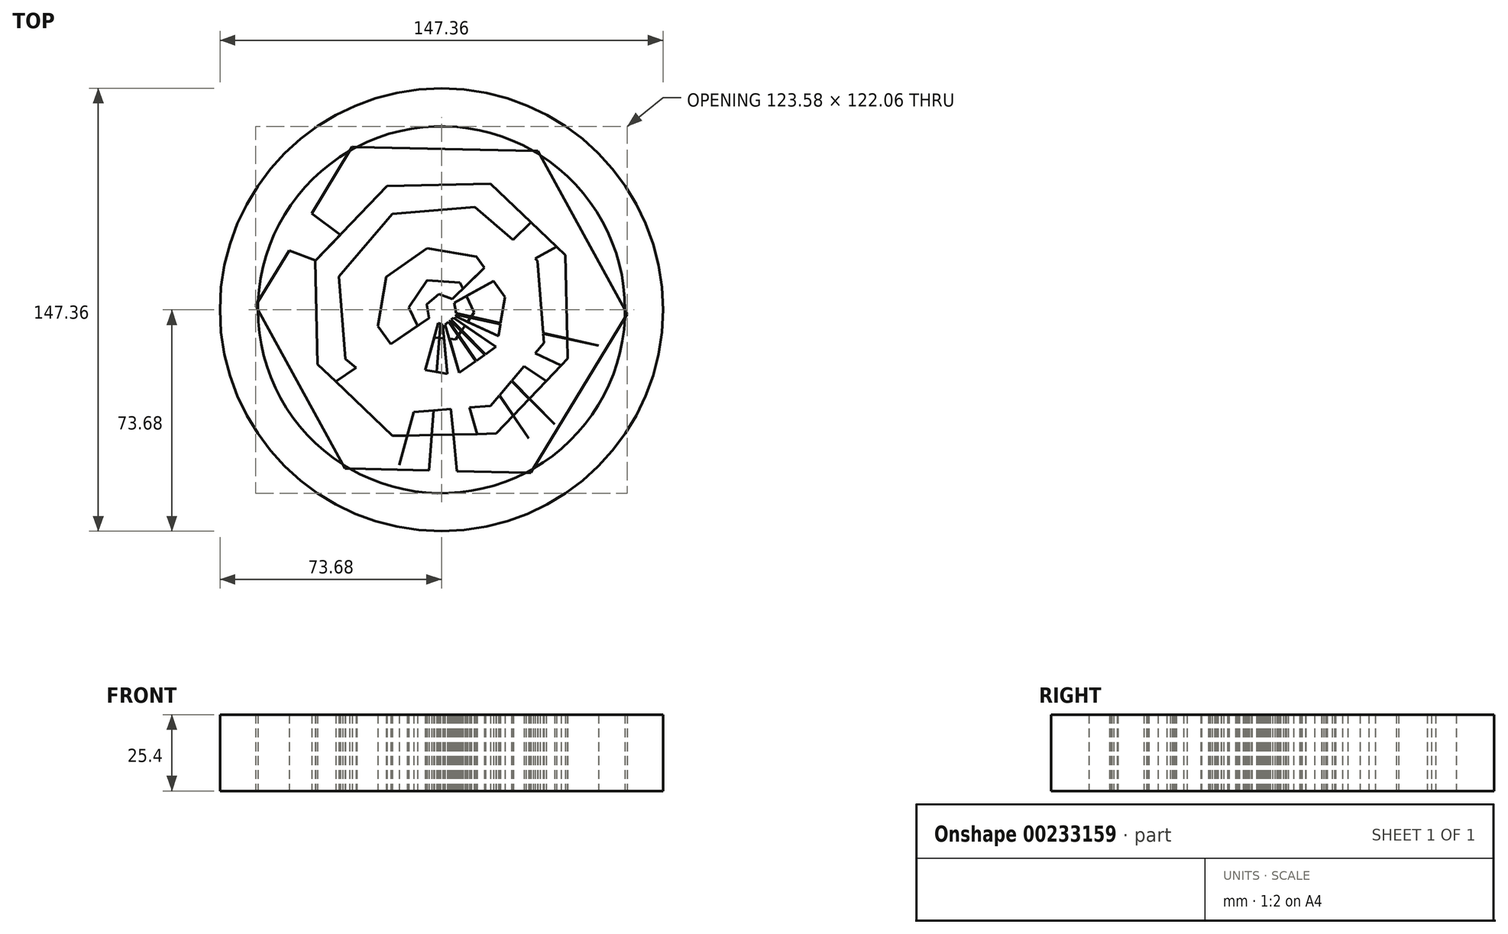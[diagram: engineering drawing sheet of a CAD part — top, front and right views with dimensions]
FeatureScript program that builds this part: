
annotation { "Feature Type Name" : "Feature", "Feature Type Description" : "" }
export const myFeature = defineFeature(function(context is Context, id is Id, definition is map)
    precondition{}
    {
        {
            var Q0;
            Q0=qCreatedBy(makeId("Top.planeOp"),FACE);
            var sketch = newSketch(context, id + "F0", { "sketchPlane" : qUnion([Q0])});
            skCircle(sketch, "E0", {"center": v(0, 0) * mm, "radius": 73.68 * mm});
            skCircle(sketch, "E1", {"center": v(0, 0) * mm, "radius": 61.04 * mm});
            skCircle(sketch, "E2.cCircle", {"center": v(0, 0) * mm, "radius": 53.52 * mm, "construction": true});
            skLineSegment(sketch, "E2.0", {"start": v(61.79, -1.37) * mm, "end": v(29.7, -54.2) * mm});
            skLineSegment(sketch, "E2.1", {"start": v(29.7, -54.2) * mm, "end": v(-32.08, -52.83) * mm});
            skLineSegment(sketch, "E2.2", {"start": v(-32.08, -52.83) * mm, "end": v(-61.79, 1.37) * mm});
            skLineSegment(sketch, "E2.3", {"start": v(-61.79, 1.37) * mm, "end": v(-29.7, 54.2) * mm});
            skLineSegment(sketch, "E2.4", {"start": v(-29.7, 54.2) * mm, "end": v(32.08, 52.83) * mm});
            skLineSegment(sketch, "E2.5", {"start": v(32.08, 52.83) * mm, "end": v(61.79, -1.37) * mm});
            skPoint(sketch, "E2.0.midPoint", {"position": v(45.75, -27.78) * mm});
            skLineSegment(sketch, "E3", {"start": v(0, 0) * mm, "end": v(-34.13, 41.23) * mm});
            skLineSegment(sketch, "E4", {"start": v(-34.13, 41.23) * mm, "end": v(-23.24, 48.21) * mm});
            skLineSegment(sketch, "E5", {"start": v(-23.24, 48.21) * mm, "end": v(0, 0) * mm});
            skLineSegment(sketch, "E6", {"start": v(-10.55, 52.47) * mm, "end": v(0, 0) * mm});
            skLineSegment(sketch, "E7", {"start": v(0, 0) * mm, "end": v(15.37, 51.27) * mm});
            skLineSegment(sketch, "E8", {"start": v(15.37, 51.27) * mm, "end": v(28.63, 45.22) * mm});
            skLineSegment(sketch, "E9", {"start": v(28.63, 45.22) * mm, "end": v(0, 0) * mm});
            skLineSegment(sketch, "E10", {"start": v(0, 0) * mm, "end": v(38.25, 37.44) * mm});
            skLineSegment(sketch, "E11", {"start": v(38.25, 37.44) * mm, "end": v(0, 0) * mm});
            skLineSegment(sketch, "E12", {"start": v(0, 0) * mm, "end": v(46.93, 25.73) * mm});
            skLineSegment(sketch, "E13", {"start": v(46.93, 25.73) * mm, "end": v(51.95, 12.87) * mm});
            skLineSegment(sketch, "E14", {"start": v(51.95, 12.87) * mm, "end": v(0, 0) * mm});
            skLineSegment(sketch, "E15", {"start": v(0, 0) * mm, "end": v(-43.18, 32) * mm});
            skLineSegment(sketch, "E16", {"start": v(-43.18, 32) * mm, "end": v(-50.62, 19.76) * mm});
            skLineSegment(sketch, "E17", {"start": v(-50.62, 19.76) * mm, "end": v(0, 0) * mm});
            skLineSegment(sketch, "E18", {"start": v(-53.16, 6.18) * mm, "end": v(0, 0) * mm});
            skLineSegment(sketch, "E19", {"start": v(-53.02, -7.3) * mm, "end": v(0, 0) * mm});
            skLineSegment(sketch, "E20", {"start": v(8.49, 53.35) * mm, "end": v(0, 0) * mm});
            skLineSegment(sketch, "E21", {"start": v(-1.18, 53.51) * mm, "end": v(0, 0) * mm});
            skPoint(sketch, "E21.startSnap0", {"position": v(1.18, 53.51) * mm});
            skLineSegment(sketch, "E22", {"start": v(-49.6, -20.1) * mm, "end": v(0, 0) * mm});
            skLineSegment(sketch, "E23", {"start": v(0, 0) * mm, "end": v(-44.46, -30.23) * mm});
            skLineSegment(sketch, "E24", {"start": v(-44.46, -30.23) * mm, "end": v(0, 0) * mm});
            skLineSegment(sketch, "E25", {"start": v(0, 0) * mm, "end": v(-38.05, -37.64) * mm});
            skLineSegment(sketch, "E26", {"start": v(-38.05, -37.64) * mm, "end": v(0, 0) * mm});
            skLineSegment(sketch, "E27", {"start": v(0, 0) * mm, "end": v(-30.17, -44.21) * mm});
            skLineSegment(sketch, "E28", {"start": v(-30.17, -44.21) * mm, "end": v(0, 0) * mm});
            skLineSegment(sketch, "E29", {"start": v(0, 0) * mm, "end": v(-22.6, -48.52) * mm});
            skLineSegment(sketch, "E30", {"start": v(-22.6, -48.52) * mm, "end": v(0, 0) * mm});
            skLineSegment(sketch, "E31", {"start": v(0, -0.62) * mm, "end": v(-14.1, -51.63) * mm});
            skLineSegment(sketch, "E32", {"start": v(-14.1, -51.63) * mm, "end": v(0, 0) * mm});
            skLineSegment(sketch, "E33", {"start": v(0, 0) * mm, "end": v(-4.14, -53.44) * mm});
            skLineSegment(sketch, "E34", {"start": v(-4.14, -53.44) * mm, "end": v(0, -0.62) * mm});
            skLineSegment(sketch, "E35", {"start": v(0, 0) * mm, "end": v(52.18, -11.9) * mm});
            skLineSegment(sketch, "E36", {"start": v(52.18, -11.9) * mm, "end": v(0, -0.62) * mm});
            skLineSegment(sketch, "E37", {"start": v(0, 0) * mm, "end": v(48.52, -22.6) * mm});
            skLineSegment(sketch, "E38", {"start": v(48.52, -22.6) * mm, "end": v(0, 0) * mm});
            skLineSegment(sketch, "E39", {"start": v(0, 0) * mm, "end": v(37.64, -38.05) * mm});
            skLineSegment(sketch, "E40", {"start": v(37.64, -38.05) * mm, "end": v(0, -0.62) * mm});
            skLineSegment(sketch, "E41", {"start": v(0, 0) * mm, "end": v(29.06, -42.74) * mm});
            skLineSegment(sketch, "E42", {"start": v(29.06, -42.74) * mm, "end": v(0, -0.62) * mm});
            skLineSegment(sketch, "E43", {"start": v(0, -0.62) * mm, "end": v(14.85, -51.42) * mm});
            skLineSegment(sketch, "E44", {"start": v(14.85, -51.42) * mm, "end": v(0, -0.62) * mm});
            skLineSegment(sketch, "E45", {"start": v(0, -0.62) * mm, "end": v(5.17, -53.65) * mm});
            skLineSegment(sketch, "E46", {"start": v(5.17, -53.65) * mm, "end": v(0, -0.62) * mm});
            skLineSegment(sketch, "E47", {"start": v(53.52, -0.62) * mm, "end": v(0, 0) * mm});
            skLineSegment(sketch, "E48", {"start": v(0, 0) * mm, "end": v(44.21, -30.17) * mm});
            skLineSegment(sketch, "E49", {"start": v(44.21, -30.17) * mm, "end": v(0, 0) * mm});
            skLineSegment(sketch, "E50", {"start": v(-53.52, -0.62) * mm, "end": v(0, 0) * mm});
            skCircle(sketch, "E51.cCircle", {"center": v(0, 0) * mm, "radius": 41.58 * mm, "construction": true});
            skLineSegment(sketch, "E51.0", {"start": v(18.14, -41.2) * mm, "end": v(-16.3, -41.95) * mm});
            skLineSegment(sketch, "E51.1", {"start": v(-16.3, -41.95) * mm, "end": v(-41.2, -18.14) * mm});
            skLineSegment(sketch, "E51.2", {"start": v(-41.2, -18.14) * mm, "end": v(-41.95, 16.3) * mm});
            skLineSegment(sketch, "E51.3", {"start": v(-41.95, 16.3) * mm, "end": v(-18.14, 41.2) * mm});
            skLineSegment(sketch, "E51.4", {"start": v(-18.14, 41.2) * mm, "end": v(16.3, 41.95) * mm});
            skLineSegment(sketch, "E51.5", {"start": v(16.3, 41.95) * mm, "end": v(41.2, 18.14) * mm});
            skLineSegment(sketch, "E51.6", {"start": v(41.2, 18.14) * mm, "end": v(41.95, -16.3) * mm});
            skLineSegment(sketch, "E51.7", {"start": v(41.95, -16.3) * mm, "end": v(18.14, -41.2) * mm});
            skPoint(sketch, "E51.0.midPoint", {"position": v(0.92, -41.57) * mm});
            skCircle(sketch, "E52.cCircle", {"center": v(0, 0) * mm, "radius": 33.14 * mm, "construction": true});
            skLineSegment(sketch, "E52.0", {"start": v(34.13, -11.05) * mm, "end": v(16.32, -31.95) * mm});
            skLineSegment(sketch, "E52.1", {"start": v(16.32, -31.95) * mm, "end": v(-11.05, -34.13) * mm});
            skLineSegment(sketch, "E52.2", {"start": v(-11.05, -34.13) * mm, "end": v(-31.95, -16.32) * mm});
            skLineSegment(sketch, "E52.3", {"start": v(-31.95, -16.32) * mm, "end": v(-34.13, 11.05) * mm});
            skLineSegment(sketch, "E52.4", {"start": v(-34.13, 11.05) * mm, "end": v(-16.32, 31.95) * mm});
            skLineSegment(sketch, "E52.5", {"start": v(-16.32, 31.95) * mm, "end": v(11.05, 34.13) * mm});
            skLineSegment(sketch, "E52.6", {"start": v(11.05, 34.13) * mm, "end": v(31.95, 16.32) * mm});
            skLineSegment(sketch, "E52.7", {"start": v(31.95, 16.32) * mm, "end": v(34.13, -11.05) * mm});
            skPoint(sketch, "E52.0.midPoint", {"position": v(25.22, -21.5) * mm});
            skCircle(sketch, "E53.cCircle", {"center": v(0, -0.62) * mm, "radius": 20.03 * mm, "construction": true});
            skLineSegment(sketch, "E53.0", {"start": v(18.32, -12.2) * mm, "end": v(4.77, -21.77) * mm});
            skLineSegment(sketch, "E53.1", {"start": v(4.77, -21.77) * mm, "end": v(-11.58, -18.94) * mm});
            skLineSegment(sketch, "E53.2", {"start": v(-11.58, -18.94) * mm, "end": v(-21.14, -5.39) * mm});
            skLineSegment(sketch, "E53.3", {"start": v(-21.14, -5.39) * mm, "end": v(-18.32, 10.96) * mm});
            skLineSegment(sketch, "E53.4", {"start": v(-18.32, 10.96) * mm, "end": v(-4.77, 20.52) * mm});
            skLineSegment(sketch, "E53.5", {"start": v(-4.77, 20.52) * mm, "end": v(11.58, 17.7) * mm});
            skLineSegment(sketch, "E53.6", {"start": v(11.58, 17.7) * mm, "end": v(21.14, 4.15) * mm});
            skLineSegment(sketch, "E53.7", {"start": v(21.14, 4.15) * mm, "end": v(18.32, -12.2) * mm});
            skPoint(sketch, "E53.0.midPoint", {"position": v(11.55, -16.98) * mm});
            skCircle(sketch, "E54.cCircle", {"center": v(0, 0) * mm, "radius": 9.46 * mm, "construction": true});
            skLineSegment(sketch, "E54.0", {"start": v(10.89, -0.82) * mm, "end": v(4.73, -9.84) * mm});
            skLineSegment(sketch, "E54.1", {"start": v(4.73, -9.84) * mm, "end": v(-6.15, -9.02) * mm});
            skLineSegment(sketch, "E54.2", {"start": v(-6.15, -9.02) * mm, "end": v(-10.89, 0.82) * mm});
            skLineSegment(sketch, "E54.3", {"start": v(-10.89, 0.82) * mm, "end": v(-4.73, 9.84) * mm});
            skLineSegment(sketch, "E54.4", {"start": v(-4.73, 9.84) * mm, "end": v(6.15, 9.02) * mm});
            skLineSegment(sketch, "E54.5", {"start": v(6.15, 9.02) * mm, "end": v(10.89, -0.82) * mm});
            skPoint(sketch, "E54.0.midPoint", {"position": v(7.81, -5.33) * mm});
            skCircle(sketch, "E55.cCircle", {"center": v(0, 0) * mm, "radius": 4.56 * mm, "construction": true});
            skLineSegment(sketch, "E55.0", {"start": v(4.93, -1.83) * mm, "end": v(0.88, -5.19) * mm});
            skLineSegment(sketch, "E55.1", {"start": v(0.88, -5.19) * mm, "end": v(-4.05, -3.35) * mm});
            skLineSegment(sketch, "E55.2", {"start": v(-4.05, -3.35) * mm, "end": v(-4.93, 1.83) * mm});
            skLineSegment(sketch, "E55.3", {"start": v(-4.93, 1.83) * mm, "end": v(-0.88, 5.19) * mm});
            skLineSegment(sketch, "E55.4", {"start": v(-0.88, 5.19) * mm, "end": v(4.05, 3.35) * mm});
            skLineSegment(sketch, "E55.5", {"start": v(4.05, 3.35) * mm, "end": v(4.93, -1.83) * mm});
            skPoint(sketch, "E55.0.midPoint", {"position": v(2.9, -3.5) * mm});
            skSolve(sketch);
        }
        {
            var Q0;
            {var subQ0=sQuery(id+"F0.wireOp",EDGE,"E53.3");var subQ3=sQuery(id+"F0.wireOp",EDGE,"E19");var subQ4=makeQuery(id+"F0.imprint","INTERSECT",VERTEX,{"derivedFrom":[subQ3,subQ0]});Q0=makeQuery(id+"F0.imprint","IMPRINT",FACE,{"disambiguationData":[TD([[makeQuery(id+"F0.imprint","IMPRINT",EDGE,{"disambiguationData":[TD([[subQ4,-1.0]])],"derivedFrom":subQ3}),-1.0]])]});}
            var Q1;
            {var subQ0=sQuery(id+"F0.wireOp",EDGE,"E53.3");var subQ1=sQuery(id+"F0.wireOp",EDGE,"E19");var subQ2=makeQuery(id+"F0.imprint","INTERSECT",VERTEX,{"derivedFrom":[subQ1,subQ0]});Q1=makeQuery(id+"F0.imprint","IMPRINT",FACE,{"disambiguationData":[TD([[makeQuery(id+"F0.imprint","IMPRINT",EDGE,{"disambiguationData":[TD([[subQ2,-1.0]])],"derivedFrom":subQ1}),1.0]])]});}
            var Q2;
            {var subQ5=sQuery(id+"F0.wireOp",EDGE,"E53.3");var subQ6=sQuery(id+"F0.wireOp",EDGE,"E18");var subQ7=makeQuery(id+"F0.imprint","INTERSECT",VERTEX,{"derivedFrom":[subQ6,subQ5]});Q2=makeQuery(id+"F0.imprint","IMPRINT",FACE,{"disambiguationData":[TD([[makeQuery(id+"F0.imprint","IMPRINT",EDGE,{"disambiguationData":[TD([[subQ7,-1.0]])],"derivedFrom":subQ6}),-1.0]])]});}
            var Q3;
            {var subQ0=sQuery(id+"F0.wireOp",EDGE,"E53.3");var subQ1=sQuery(id+"F0.wireOp",EDGE,"E17");var subQ2=makeQuery(id+"F0.imprint","INTERSECT",VERTEX,{"derivedFrom":[subQ1,subQ0]});Q3=makeQuery(id+"F0.imprint","IMPRINT",FACE,{"disambiguationData":[TD([[makeQuery(id+"F0.imprint","IMPRINT",EDGE,{"disambiguationData":[TD([[subQ2,-1.0]])],"derivedFrom":subQ1}),-1.0]])]});}
            var Q4;
            {var subQ3=sQuery(id+"F0.wireOp",EDGE,"E15");var subQ7=sQuery(id+"F0.wireOp",EDGE,"E54.3");var subQ9=makeQuery(id+"F0.imprint","INTERSECT",VERTEX,{"derivedFrom":[subQ3,subQ7]});Q4=makeQuery(id+"F0.imprint","IMPRINT",FACE,{"disambiguationData":[TD([[makeQuery(id+"F0.imprint","IMPRINT",EDGE,{"disambiguationData":[TD([[subQ9,-1.0]])],"derivedFrom":subQ3}),1.0]])]});}
            var Q5;
            {var subQ0=sQuery(id+"F0.wireOp",EDGE,"E54.3");var subQ1=sQuery(id+"F0.wireOp",EDGE,"E3");var subQ2=makeQuery(id+"F0.imprint","INTERSECT",VERTEX,{"derivedFrom":[subQ1,subQ0]});Q5=makeQuery(id+"F0.imprint","IMPRINT",FACE,{"disambiguationData":[TD([[makeQuery(id+"F0.imprint","IMPRINT",EDGE,{"disambiguationData":[TD([[subQ2,-1.0]])],"derivedFrom":subQ1}),1.0]])]});}
            var Q6;
            {var subQ0=sQuery(id+"F0.wireOp",EDGE,"E54.3");var subQ1=sQuery(id+"F0.wireOp",EDGE,"E3");var subQ2=makeQuery(id+"F0.imprint","INTERSECT",VERTEX,{"derivedFrom":[subQ1,subQ0]});Q6=makeQuery(id+"F0.imprint","IMPRINT",FACE,{"disambiguationData":[TD([[makeQuery(id+"F0.imprint","IMPRINT",EDGE,{"disambiguationData":[TD([[subQ2,-1.0]])],"derivedFrom":subQ1}),-1.0]])]});}
            var Q7;
            {var subQ1=sQuery(id+"F0.wireOp",EDGE,"E53.4");var subQ7=sQuery(id+"F0.wireOp",EDGE,"E5");var subQ8=makeQuery(id+"F0.imprint","INTERSECT",VERTEX,{"derivedFrom":[subQ7,subQ1]});Q7=makeQuery(id+"F0.imprint","IMPRINT",FACE,{"disambiguationData":[TD([[makeQuery(id+"F0.imprint","IMPRINT",EDGE,{"disambiguationData":[TD([[subQ8,-1.0]])],"derivedFrom":subQ7}),1.0]])]});}
            var Q8;
            {var subQ0=sQuery(id+"F0.wireOp",EDGE,"E53.5");var subQ1=sQuery(id+"F0.wireOp",EDGE,"E6");var subQ2=makeQuery(id+"F0.imprint","INTERSECT",VERTEX,{"derivedFrom":[subQ1,subQ0]});Q8=makeQuery(id+"F0.imprint","IMPRINT",FACE,{"disambiguationData":[TD([[makeQuery(id+"F0.imprint","IMPRINT",EDGE,{"disambiguationData":[TD([[subQ2,-1.0]])],"derivedFrom":subQ1}),1.0]])]});}
            var Q9;
            {var subQ0=sQuery(id+"F0.wireOp",EDGE,"E53.5");var subQ1=sQuery(id+"F0.wireOp",EDGE,"E20");var subQ2=makeQuery(id+"F0.imprint","INTERSECT",VERTEX,{"derivedFrom":[subQ1,subQ0]});Q9=makeQuery(id+"F0.imprint","IMPRINT",FACE,{"disambiguationData":[TD([[makeQuery(id+"F0.imprint","IMPRINT",EDGE,{"disambiguationData":[TD([[subQ2,-1.0]])],"derivedFrom":subQ1}),-1.0]])]});}
            var Q10;
            {var subQ0=sQuery(id+"F0.wireOp",EDGE,"E54.4");var subQ1=sQuery(id+"F0.wireOp",EDGE,"E7");var subQ2=makeQuery(id+"F0.imprint","INTERSECT",VERTEX,{"derivedFrom":[subQ1,subQ0]});Q10=makeQuery(id+"F0.imprint","IMPRINT",FACE,{"disambiguationData":[TD([[makeQuery(id+"F0.imprint","IMPRINT",EDGE,{"disambiguationData":[TD([[subQ2,-1.0]])],"derivedFrom":subQ1}),1.0]])]});}
            var Q11;
            {var subQ0=sQuery(id+"F0.wireOp",EDGE,"E54.4");var subQ1=sQuery(id+"F0.wireOp",EDGE,"E7");var subQ2=makeQuery(id+"F0.imprint","INTERSECT",VERTEX,{"derivedFrom":[subQ1,subQ0]});Q11=makeQuery(id+"F0.imprint","IMPRINT",FACE,{"disambiguationData":[TD([[makeQuery(id+"F0.imprint","IMPRINT",EDGE,{"disambiguationData":[TD([[subQ2,-1.0]])],"derivedFrom":subQ1}),-1.0]])]});}
            var Q12;
            {var subQ1=sQuery(id+"F0.wireOp",EDGE,"E53.5");var subQ5=sQuery(id+"F0.wireOp",EDGE,"E9");var subQ6=makeQuery(id+"F0.imprint","INTERSECT",VERTEX,{"derivedFrom":[subQ5,subQ1]});Q12=makeQuery(id+"F0.imprint","IMPRINT",FACE,{"disambiguationData":[TD([[makeQuery(id+"F0.imprint","IMPRINT",EDGE,{"disambiguationData":[TD([[subQ6,-1.0]])],"derivedFrom":subQ5}),1.0]])]});}
            var Q13;
            {var subQ0=sQuery(id+"F0.wireOp",EDGE,"E53.6");var subQ1=sQuery(id+"F0.wireOp",EDGE,"E11");var subQ2=makeQuery(id+"F0.imprint","INTERSECT",VERTEX,{"derivedFrom":[subQ1,subQ0]});Q13=makeQuery(id+"F0.imprint","IMPRINT",FACE,{"disambiguationData":[TD([[makeQuery(id+"F0.imprint","IMPRINT",EDGE,{"disambiguationData":[TD([[subQ2,-1.0]])],"derivedFrom":subQ1}),1.0]])]});}
            var Q14;
            {var subQ1=sQuery(id+"F0.wireOp",EDGE,"E54.0");var subQ3=sQuery(id+"F0.wireOp",EDGE,"E35");var subQ4=makeQuery(id+"F0.imprint","INTERSECT",VERTEX,{"derivedFrom":[subQ3,subQ1]});Q14=makeQuery(id+"F0.imprint","IMPRINT",FACE,{"disambiguationData":[TD([[makeQuery(id+"F0.imprint","IMPRINT",EDGE,{"disambiguationData":[TD([[subQ4,-1.0]])],"derivedFrom":subQ3}),1.0]])]});}
            var Q15;
            {var subQ0=sQuery(id+"F0.wireOp",EDGE,"E54.5");var subQ1=sQuery(id+"F0.wireOp",EDGE,"E12");var subQ2=makeQuery(id+"F0.imprint","INTERSECT",VERTEX,{"derivedFrom":[subQ1,subQ0]});Q15=makeQuery(id+"F0.imprint","IMPRINT",FACE,{"disambiguationData":[TD([[makeQuery(id+"F0.imprint","IMPRINT",EDGE,{"disambiguationData":[TD([[subQ2,-1.0]])],"derivedFrom":subQ1}),-1.0]])]});}
            var Q16;
            {var subQ1=sQuery(id+"F0.wireOp",EDGE,"E53.6");var subQ3=sQuery(id+"F0.wireOp",EDGE,"E14");var subQ4=makeQuery(id+"F0.imprint","INTERSECT",VERTEX,{"derivedFrom":[subQ3,subQ1]});Q16=makeQuery(id+"F0.imprint","IMPRINT",FACE,{"disambiguationData":[TD([[makeQuery(id+"F0.imprint","IMPRINT",EDGE,{"disambiguationData":[TD([[subQ4,-1.0]])],"derivedFrom":subQ3}),1.0]])]});}
            var Q17;
            {var subQ5=sQuery(id+"F0.wireOp",EDGE,"E35");var subQ7=sQuery(id+"F0.wireOp",EDGE,"E55.5");var subQ9=makeQuery(id+"F0.imprint","INTERSECT",VERTEX,{"derivedFrom":[subQ5,subQ7]});Q17=makeQuery(id+"F0.imprint","IMPRINT",FACE,{"disambiguationData":[TD([[makeQuery(id+"F0.imprint","IMPRINT",EDGE,{"disambiguationData":[TD([[subQ9,-1.0]])],"derivedFrom":subQ5}),1.0]])]});}
            var Q18;
            {var subQ0=sQuery(id+"F0.wireOp",EDGE,"E54.5");var subQ1=sQuery(id+"F0.wireOp",EDGE,"E14");var subQ2=makeQuery(id+"F0.imprint","INTERSECT",VERTEX,{"derivedFrom":[subQ1,subQ0]});Q18=makeQuery(id+"F0.imprint","IMPRINT",FACE,{"disambiguationData":[TD([[makeQuery(id+"F0.imprint","IMPRINT",EDGE,{"disambiguationData":[TD([[subQ2,-1.0]])],"derivedFrom":subQ1}),1.0]])]});}
            var Q19;
            {var subQ0=sQuery(id+"F0.wireOp",EDGE,"E55.5");var subQ1=sQuery(id+"F0.wireOp",EDGE,"E12");var subQ2=makeQuery(id+"F0.imprint","INTERSECT",VERTEX,{"derivedFrom":[subQ1,subQ0]});Q19=makeQuery(id+"F0.imprint","IMPRINT",FACE,{"disambiguationData":[TD([[makeQuery(id+"F0.imprint","IMPRINT",EDGE,{"disambiguationData":[TD([[subQ2,-1.0]])],"derivedFrom":subQ1}),-1.0]])]});}
            var Q20;
            {var subQ3=sQuery(id+"F0.wireOp",EDGE,"E11");var subQ5=sQuery(id+"F0.wireOp",EDGE,"E54.5");var subQ6=makeQuery(id+"F0.imprint","INTERSECT",VERTEX,{"derivedFrom":[subQ3,subQ5]});Q20=makeQuery(id+"F0.imprint","IMPRINT",FACE,{"disambiguationData":[TD([[makeQuery(id+"F0.imprint","IMPRINT",EDGE,{"disambiguationData":[TD([[subQ6,-1.0]])],"derivedFrom":subQ3}),1.0]])]});}
            var Q21;
            {var subQ1=sQuery(id+"F0.wireOp",EDGE,"E54.4");var subQ6=sQuery(id+"F0.wireOp",EDGE,"E9");var subQ9=makeQuery(id+"F0.imprint","INTERSECT",VERTEX,{"derivedFrom":[subQ6,subQ1]});Q21=makeQuery(id+"F0.imprint","IMPRINT",FACE,{"disambiguationData":[TD([[makeQuery(id+"F0.imprint","IMPRINT",EDGE,{"disambiguationData":[TD([[subQ9,-1.0]])],"derivedFrom":subQ6}),1.0]])]});}
            var Q22;
            {var subQ0=sQuery(id+"F0.wireOp",EDGE,"E55.4");var subQ1=sQuery(id+"F0.wireOp",EDGE,"E7");var subQ2=makeQuery(id+"F0.imprint","INTERSECT",VERTEX,{"derivedFrom":[subQ1,subQ0]});Q22=makeQuery(id+"F0.imprint","IMPRINT",FACE,{"disambiguationData":[TD([[makeQuery(id+"F0.imprint","IMPRINT",EDGE,{"disambiguationData":[TD([[subQ2,-1.0]])],"derivedFrom":subQ1}),-1.0]])]});}
            var Q23;
            {var subQ0=sQuery(id+"F0.wireOp",EDGE,"E55.4");var subQ1=sQuery(id+"F0.wireOp",EDGE,"E7");var subQ2=makeQuery(id+"F0.imprint","INTERSECT",VERTEX,{"derivedFrom":[subQ1,subQ0]});Q23=makeQuery(id+"F0.imprint","IMPRINT",FACE,{"disambiguationData":[TD([[makeQuery(id+"F0.imprint","IMPRINT",EDGE,{"disambiguationData":[TD([[subQ2,-1.0]])],"derivedFrom":subQ1}),1.0]])]});}
            var Q24;
            {var subQ0=sQuery(id+"F0.wireOp",EDGE,"E54.4");var subQ1=sQuery(id+"F0.wireOp",EDGE,"E20");var subQ2=makeQuery(id+"F0.imprint","INTERSECT",VERTEX,{"derivedFrom":[subQ1,subQ0]});Q24=makeQuery(id+"F0.imprint","IMPRINT",FACE,{"disambiguationData":[TD([[makeQuery(id+"F0.imprint","IMPRINT",EDGE,{"disambiguationData":[TD([[subQ2,-1.0]])],"derivedFrom":subQ1}),-1.0]])]});}
            var Q25;
            {var subQ3=sQuery(id+"F0.wireOp",EDGE,"E6");var subQ5=sQuery(id+"F0.wireOp",EDGE,"E54.4");var subQ6=makeQuery(id+"F0.imprint","INTERSECT",VERTEX,{"derivedFrom":[subQ3,subQ5]});Q25=makeQuery(id+"F0.imprint","IMPRINT",FACE,{"disambiguationData":[TD([[makeQuery(id+"F0.imprint","IMPRINT",EDGE,{"disambiguationData":[TD([[subQ6,-1.0]])],"derivedFrom":subQ3}),1.0]])]});}
            var Q26;
            {var subQ1=sQuery(id+"F0.wireOp",EDGE,"E54.3");var subQ6=sQuery(id+"F0.wireOp",EDGE,"E5");var subQ9=makeQuery(id+"F0.imprint","INTERSECT",VERTEX,{"derivedFrom":[subQ6,subQ1]});Q26=makeQuery(id+"F0.imprint","IMPRINT",FACE,{"disambiguationData":[TD([[makeQuery(id+"F0.imprint","IMPRINT",EDGE,{"disambiguationData":[TD([[subQ9,-1.0]])],"derivedFrom":subQ6}),1.0]])]});}
            var Q27;
            {var subQ0=sQuery(id+"F0.wireOp",EDGE,"E55.3");var subQ1=sQuery(id+"F0.wireOp",EDGE,"E3");var subQ2=makeQuery(id+"F0.imprint","INTERSECT",VERTEX,{"derivedFrom":[subQ1,subQ0]});Q27=makeQuery(id+"F0.imprint","IMPRINT",FACE,{"disambiguationData":[TD([[makeQuery(id+"F0.imprint","IMPRINT",EDGE,{"disambiguationData":[TD([[subQ2,-1.0]])],"derivedFrom":subQ1}),-1.0]])]});}
            var Q28;
            {var subQ0=sQuery(id+"F0.wireOp",EDGE,"E55.3");var subQ1=sQuery(id+"F0.wireOp",EDGE,"E3");var subQ2=makeQuery(id+"F0.imprint","INTERSECT",VERTEX,{"derivedFrom":[subQ1,subQ0]});Q28=makeQuery(id+"F0.imprint","IMPRINT",FACE,{"disambiguationData":[TD([[makeQuery(id+"F0.imprint","IMPRINT",EDGE,{"disambiguationData":[TD([[subQ2,-1.0]])],"derivedFrom":subQ1}),1.0]])]});}
            var Q29;
            {var subQ0=sQuery(id+"F0.wireOp",EDGE,"E55.3");var subQ1=sQuery(id+"F0.wireOp",EDGE,"E15");var subQ2=makeQuery(id+"F0.imprint","INTERSECT",VERTEX,{"derivedFrom":[subQ1,subQ0]});Q29=makeQuery(id+"F0.imprint","IMPRINT",FACE,{"disambiguationData":[TD([[makeQuery(id+"F0.imprint","IMPRINT",EDGE,{"disambiguationData":[TD([[subQ2,-1.0]])],"derivedFrom":subQ1}),1.0]])]});}
            var Q30;
            {var subQ0=sQuery(id+"F0.wireOp",EDGE,"E54.3");var subQ1=sQuery(id+"F0.wireOp",EDGE,"E17");var subQ2=makeQuery(id+"F0.imprint","INTERSECT",VERTEX,{"derivedFrom":[subQ1,subQ0]});Q30=makeQuery(id+"F0.imprint","IMPRINT",FACE,{"disambiguationData":[TD([[makeQuery(id+"F0.imprint","IMPRINT",EDGE,{"disambiguationData":[TD([[subQ2,-1.0]])],"derivedFrom":subQ1}),-1.0]])]});}
            var Q31;
            {var subQ0=sQuery(id+"F0.wireOp",EDGE,"E54.2");var subQ1=sQuery(id+"F0.wireOp",EDGE,"E19");var subQ2=makeQuery(id+"F0.imprint","INTERSECT",VERTEX,{"derivedFrom":[subQ1,subQ0]});Q31=makeQuery(id+"F0.imprint","IMPRINT",FACE,{"disambiguationData":[TD([[makeQuery(id+"F0.imprint","IMPRINT",EDGE,{"disambiguationData":[TD([[subQ2,-1.0]])],"derivedFrom":subQ1}),1.0]])]});}
            var Q32;
            {var subQ0=sQuery(id+"F0.wireOp",EDGE,"E54.3");var subQ3=sQuery(id+"F0.wireOp",EDGE,"E18");var subQ4=makeQuery(id+"F0.imprint","INTERSECT",VERTEX,{"derivedFrom":[subQ3,subQ0]});Q32=makeQuery(id+"F0.imprint","IMPRINT",FACE,{"disambiguationData":[TD([[makeQuery(id+"F0.imprint","IMPRINT",EDGE,{"disambiguationData":[TD([[subQ4,-1.0]])],"derivedFrom":subQ3}),-1.0]])]});}
            var Q33;
            {var subQ0=sQuery(id+"F0.wireOp",EDGE,"E54.2");var subQ1=sQuery(id+"F0.wireOp",EDGE,"E19");var subQ2=makeQuery(id+"F0.imprint","INTERSECT",VERTEX,{"derivedFrom":[subQ1,subQ0]});Q33=makeQuery(id+"F0.imprint","IMPRINT",FACE,{"disambiguationData":[TD([[makeQuery(id+"F0.imprint","IMPRINT",EDGE,{"disambiguationData":[TD([[subQ2,-1.0]])],"derivedFrom":subQ1}),-1.0]])]});}
            var Q34;
            {var subQ0=sQuery(id+"F0.wireOp",EDGE,"E54.2");var subQ1=sQuery(id+"F0.wireOp",EDGE,"E22");var subQ2=makeQuery(id+"F0.imprint","INTERSECT",VERTEX,{"derivedFrom":[subQ1,subQ0]});Q34=makeQuery(id+"F0.imprint","IMPRINT",FACE,{"disambiguationData":[TD([[makeQuery(id+"F0.imprint","IMPRINT",EDGE,{"disambiguationData":[TD([[subQ2,-1.0]])],"derivedFrom":subQ1}),-1.0]])]});}
            var Q35;
            {var subQ0=sQuery(id+"F0.wireOp",EDGE,"E54.2");var subQ1=sQuery(id+"F0.wireOp",EDGE,"E24");var subQ2=makeQuery(id+"F0.imprint","INTERSECT",VERTEX,{"derivedFrom":[subQ1,subQ0]});Q35=makeQuery(id+"F0.imprint","IMPRINT",FACE,{"disambiguationData":[TD([[makeQuery(id+"F0.imprint","IMPRINT",EDGE,{"disambiguationData":[TD([[subQ2,-1.0]])],"derivedFrom":subQ1}),-1.0]])]});}
            var Q36;
            {var subQ0=sQuery(id+"F0.wireOp",EDGE,"E54.2");var subQ1=sQuery(id+"F0.wireOp",EDGE,"E26");var subQ2=makeQuery(id+"F0.imprint","INTERSECT",VERTEX,{"derivedFrom":[subQ1,subQ0]});Q36=makeQuery(id+"F0.imprint","IMPRINT",FACE,{"disambiguationData":[TD([[makeQuery(id+"F0.imprint","IMPRINT",EDGE,{"disambiguationData":[TD([[subQ2,-1.0]])],"derivedFrom":subQ1}),-1.0]])]});}
            var Q37;
            {var subQ0=sQuery(id+"F0.wireOp",EDGE,"E54.1");var subQ5=sQuery(id+"F0.wireOp",EDGE,"E30");var subQ6=makeQuery(id+"F0.imprint","INTERSECT",VERTEX,{"derivedFrom":[subQ5,subQ0]});Q37=makeQuery(id+"F0.imprint","IMPRINT",FACE,{"disambiguationData":[TD([[makeQuery(id+"F0.imprint","IMPRINT",EDGE,{"disambiguationData":[TD([[subQ6,-1.0]])],"derivedFrom":subQ5}),1.0]])]});}
            var Q38;
            {var subQ0=sQuery(id+"F0.wireOp",EDGE,"E54.1");var subQ1=sQuery(id+"F0.wireOp",EDGE,"E30");var subQ2=makeQuery(id+"F0.imprint","INTERSECT",VERTEX,{"derivedFrom":[subQ1,subQ0]});Q38=makeQuery(id+"F0.imprint","IMPRINT",FACE,{"disambiguationData":[TD([[makeQuery(id+"F0.imprint","IMPRINT",EDGE,{"disambiguationData":[TD([[subQ2,-1.0]])],"derivedFrom":subQ1}),-1.0]])]});}
            var Q39;
            {var subQ0=sQuery(id+"F0.wireOp",EDGE,"E55.1");var subQ1=sQuery(id+"F0.wireOp",EDGE,"E31");var subQ2=makeQuery(id+"F0.imprint","INTERSECT",VERTEX,{"derivedFrom":[subQ1,subQ0]});Q39=makeQuery(id+"F0.imprint","IMPRINT",FACE,{"disambiguationData":[TD([[makeQuery(id+"F0.imprint","IMPRINT",EDGE,{"disambiguationData":[TD([[subQ2,-1.0]])],"derivedFrom":subQ1}),1.0]])]});}
            var Q40;
            {var subQ0=sQuery(id+"F0.wireOp",EDGE,"E54.1");var subQ1=sQuery(id+"F0.wireOp",EDGE,"E44");var subQ2=makeQuery(id+"F0.imprint","INTERSECT",VERTEX,{"derivedFrom":[subQ1,subQ0]});Q40=makeQuery(id+"F0.imprint","IMPRINT",FACE,{"disambiguationData":[TD([[makeQuery(id+"F0.imprint","IMPRINT",EDGE,{"disambiguationData":[TD([[subQ2,-1.0]])],"derivedFrom":subQ1}),1.0]])]});}
            var Q41;
            {var subQ0=sQuery(id+"F0.wireOp",EDGE,"E54.1");var subQ1=sQuery(id+"F0.wireOp",EDGE,"E34");var subQ2=makeQuery(id+"F0.imprint","INTERSECT",VERTEX,{"derivedFrom":[subQ1,subQ0]});Q41=makeQuery(id+"F0.imprint","IMPRINT",FACE,{"disambiguationData":[TD([[makeQuery(id+"F0.imprint","IMPRINT",EDGE,{"disambiguationData":[TD([[subQ2,-1.0]])],"derivedFrom":subQ1}),-1.0]])]});}
            var Q42;
            {var subQ1=sQuery(id+"F0.wireOp",EDGE,"E54.0");var subQ5=sQuery(id+"F0.wireOp",EDGE,"E42");var subQ6=makeQuery(id+"F0.imprint","INTERSECT",VERTEX,{"derivedFrom":[subQ5,subQ1]});Q42=makeQuery(id+"F0.imprint","IMPRINT",FACE,{"disambiguationData":[TD([[makeQuery(id+"F0.imprint","IMPRINT",EDGE,{"disambiguationData":[TD([[subQ6,-1.0]])],"derivedFrom":subQ5}),1.0]])]});}
            var Q43;
            {var subQ0=sQuery(id+"F0.wireOp",EDGE,"E54.0");var subQ1=sQuery(id+"F0.wireOp",EDGE,"E40");var subQ2=makeQuery(id+"F0.imprint","INTERSECT",VERTEX,{"derivedFrom":[subQ1,subQ0]});Q43=makeQuery(id+"F0.imprint","IMPRINT",FACE,{"disambiguationData":[TD([[makeQuery(id+"F0.imprint","IMPRINT",EDGE,{"disambiguationData":[TD([[subQ2,-1.0]])],"derivedFrom":subQ1}),1.0]])]});}
            var Q44;
            {var subQ0=sQuery(id+"F0.wireOp",EDGE,"E55.0");var subQ1=sQuery(id+"F0.wireOp",EDGE,"E39");var subQ2=makeQuery(id+"F0.imprint","INTERSECT",VERTEX,{"derivedFrom":[subQ1,subQ0]});Q44=makeQuery(id+"F0.imprint","IMPRINT",FACE,{"disambiguationData":[TD([[makeQuery(id+"F0.imprint","IMPRINT",EDGE,{"disambiguationData":[TD([[subQ2,-1.0]])],"derivedFrom":subQ1}),1.0]])]});}
            var Q45;
            {var subQ5=sQuery(id+"F0.wireOp",EDGE,"E54.0");var subQ6=sQuery(id+"F0.wireOp",EDGE,"E36");var subQ7=makeQuery(id+"F0.imprint","INTERSECT",VERTEX,{"derivedFrom":[subQ6,subQ5]});Q45=makeQuery(id+"F0.imprint","IMPRINT",FACE,{"disambiguationData":[TD([[makeQuery(id+"F0.imprint","IMPRINT",EDGE,{"disambiguationData":[TD([[subQ7,-1.0]])],"derivedFrom":subQ6}),1.0]])]});}
            var Q46;
            {var subQ0=sQuery(id+"F0.wireOp",EDGE,"E54.0");var subQ1=sQuery(id+"F0.wireOp",EDGE,"E38");var subQ2=makeQuery(id+"F0.imprint","INTERSECT",VERTEX,{"derivedFrom":[subQ1,subQ0]});Q46=makeQuery(id+"F0.imprint","IMPRINT",FACE,{"disambiguationData":[TD([[makeQuery(id+"F0.imprint","IMPRINT",EDGE,{"disambiguationData":[TD([[subQ2,-1.0]])],"derivedFrom":subQ1}),1.0]])]});}
            var Q47;
            {var subQ0=sQuery(id+"F0.wireOp",EDGE,"E53.2");var subQ1=sQuery(id+"F0.wireOp",EDGE,"E22");var subQ2=makeQuery(id+"F0.imprint","INTERSECT",VERTEX,{"derivedFrom":[subQ1,subQ0]});Q47=makeQuery(id+"F0.imprint","IMPRINT",FACE,{"disambiguationData":[TD([[makeQuery(id+"F0.imprint","IMPRINT",EDGE,{"disambiguationData":[TD([[subQ2,-1.0]])],"derivedFrom":subQ1}),-1.0]])]});}
            var Q48;
            {var subQ0=sQuery(id+"F0.wireOp",EDGE,"E53.2");var subQ1=sQuery(id+"F0.wireOp",EDGE,"E26");var subQ2=makeQuery(id+"F0.imprint","INTERSECT",VERTEX,{"derivedFrom":[subQ1,subQ0]});Q48=makeQuery(id+"F0.imprint","IMPRINT",FACE,{"disambiguationData":[TD([[makeQuery(id+"F0.imprint","IMPRINT",EDGE,{"disambiguationData":[TD([[subQ2,-1.0]])],"derivedFrom":subQ1}),-1.0]])]});}
            var Q49;
            {var subQ1=sQuery(id+"F0.wireOp",EDGE,"E53.1");var subQ5=sQuery(id+"F0.wireOp",EDGE,"E30");var subQ6=makeQuery(id+"F0.imprint","INTERSECT",VERTEX,{"derivedFrom":[subQ5,subQ1]});Q49=makeQuery(id+"F0.imprint","IMPRINT",FACE,{"disambiguationData":[TD([[makeQuery(id+"F0.imprint","IMPRINT",EDGE,{"disambiguationData":[TD([[subQ6,-1.0]])],"derivedFrom":subQ5}),1.0]])]});}
            var Q50;
            {var subQ0=sQuery(id+"F0.wireOp",EDGE,"E53.1");var subQ1=sQuery(id+"F0.wireOp",EDGE,"E30");var subQ2=makeQuery(id+"F0.imprint","INTERSECT",VERTEX,{"derivedFrom":[subQ1,subQ0]});Q50=makeQuery(id+"F0.imprint","IMPRINT",FACE,{"disambiguationData":[TD([[makeQuery(id+"F0.imprint","IMPRINT",EDGE,{"disambiguationData":[TD([[subQ2,-1.0]])],"derivedFrom":subQ1}),-1.0]])]});}
            var Q51;
            {var subQ0=sQuery(id+"F0.wireOp",EDGE,"E54.1");var subQ1=sQuery(id+"F0.wireOp",EDGE,"E31");var subQ2=makeQuery(id+"F0.imprint","INTERSECT",VERTEX,{"derivedFrom":[subQ1,subQ0]});Q51=makeQuery(id+"F0.imprint","IMPRINT",FACE,{"disambiguationData":[TD([[makeQuery(id+"F0.imprint","IMPRINT",EDGE,{"disambiguationData":[TD([[subQ2,-1.0]])],"derivedFrom":subQ1}),1.0]])]});}
            var Q52;
            {var subQ0=sQuery(id+"F0.wireOp",EDGE,"E53.1");var subQ1=sQuery(id+"F0.wireOp",EDGE,"E34");var subQ2=makeQuery(id+"F0.imprint","INTERSECT",VERTEX,{"derivedFrom":[subQ1,subQ0]});Q52=makeQuery(id+"F0.imprint","IMPRINT",FACE,{"disambiguationData":[TD([[makeQuery(id+"F0.imprint","IMPRINT",EDGE,{"disambiguationData":[TD([[subQ2,-1.0]])],"derivedFrom":subQ1}),-1.0]])]});}
            var Q53;
            {var subQ1=sQuery(id+"F0.wireOp",EDGE,"E53.0");var subQ5=sQuery(id+"F0.wireOp",EDGE,"E44");var subQ6=makeQuery(id+"F0.imprint","INTERSECT",VERTEX,{"derivedFrom":[subQ5,subQ1]});Q53=makeQuery(id+"F0.imprint","IMPRINT",FACE,{"disambiguationData":[TD([[makeQuery(id+"F0.imprint","IMPRINT",EDGE,{"disambiguationData":[TD([[subQ6,-1.0]])],"derivedFrom":subQ5}),1.0]])]});}
            var Q54;
            {var subQ3=sQuery(id+"F0.wireOp",EDGE,"E42");var subQ5=sQuery(id+"F0.wireOp",EDGE,"E53.0");var subQ6=makeQuery(id+"F0.imprint","INTERSECT",VERTEX,{"derivedFrom":[subQ3,subQ5]});Q54=makeQuery(id+"F0.imprint","IMPRINT",FACE,{"disambiguationData":[TD([[makeQuery(id+"F0.imprint","IMPRINT",EDGE,{"disambiguationData":[TD([[subQ6,-1.0]])],"derivedFrom":subQ3}),1.0]])]});}
            var Q55;
            {var subQ0=sQuery(id+"F0.wireOp",EDGE,"E53.0");var subQ1=sQuery(id+"F0.wireOp",EDGE,"E40");var subQ2=makeQuery(id+"F0.imprint","INTERSECT",VERTEX,{"derivedFrom":[subQ1,subQ0]});Q55=makeQuery(id+"F0.imprint","IMPRINT",FACE,{"disambiguationData":[TD([[makeQuery(id+"F0.imprint","IMPRINT",EDGE,{"disambiguationData":[TD([[subQ2,-1.0]])],"derivedFrom":subQ1}),1.0]])]});}
            var Q56;
            {var subQ0=sQuery(id+"F0.wireOp",EDGE,"E54.0");var subQ1=sQuery(id+"F0.wireOp",EDGE,"E39");var subQ2=makeQuery(id+"F0.imprint","INTERSECT",VERTEX,{"derivedFrom":[subQ1,subQ0]});Q56=makeQuery(id+"F0.imprint","IMPRINT",FACE,{"disambiguationData":[TD([[makeQuery(id+"F0.imprint","IMPRINT",EDGE,{"disambiguationData":[TD([[subQ2,-1.0]])],"derivedFrom":subQ1}),1.0]])]});}
            var Q57;
            {var subQ0=sQuery(id+"F0.wireOp",EDGE,"E53.7");var subQ3=sQuery(id+"F0.wireOp",EDGE,"E38");var subQ4=makeQuery(id+"F0.imprint","INTERSECT",VERTEX,{"derivedFrom":[subQ3,subQ0]});Q57=makeQuery(id+"F0.imprint","IMPRINT",FACE,{"disambiguationData":[TD([[makeQuery(id+"F0.imprint","IMPRINT",EDGE,{"disambiguationData":[TD([[subQ4,-1.0]])],"derivedFrom":subQ3}),1.0]])]});}
            var Q58;
            {var subQ0=sQuery(id+"F0.wireOp",EDGE,"E53.7");var subQ1=sQuery(id+"F0.wireOp",EDGE,"E36");var subQ2=makeQuery(id+"F0.imprint","INTERSECT",VERTEX,{"derivedFrom":[subQ1,subQ0]});Q58=makeQuery(id+"F0.imprint","IMPRINT",FACE,{"disambiguationData":[TD([[makeQuery(id+"F0.imprint","IMPRINT",EDGE,{"disambiguationData":[TD([[subQ2,-1.0]])],"derivedFrom":subQ1}),1.0]])]});}
            var Q59;
            {var subQ0=sQuery(id+"F0.wireOp",EDGE,"E53.2");var subQ1=sQuery(id+"F0.wireOp",EDGE,"E24");var subQ2=makeQuery(id+"F0.imprint","INTERSECT",VERTEX,{"derivedFrom":[subQ1,subQ0]});Q59=makeQuery(id+"F0.imprint","IMPRINT",FACE,{"disambiguationData":[TD([[makeQuery(id+"F0.imprint","IMPRINT",EDGE,{"disambiguationData":[TD([[subQ2,-1.0]])],"derivedFrom":subQ1}),-1.0]])]});}
            var Q60;
            {var subQ0=sQuery(id+"F0.wireOp",EDGE,"E52.4");var subQ1=sQuery(id+"F0.wireOp",EDGE,"E3");var subQ2=makeQuery(id+"F0.imprint","INTERSECT",VERTEX,{"derivedFrom":[subQ1,subQ0]});Q60=makeQuery(id+"F0.imprint","IMPRINT",FACE,{"disambiguationData":[TD([[makeQuery(id+"F0.imprint","IMPRINT",EDGE,{"disambiguationData":[TD([[subQ2,-1.0]])],"derivedFrom":subQ1}),1.0]])]});}
            var Q61;
            {var subQ1=sQuery(id+"F0.wireOp",EDGE,"E52.4");var subQ3=sQuery(id+"F0.wireOp",EDGE,"E3");var subQ4=makeQuery(id+"F0.imprint","INTERSECT",VERTEX,{"derivedFrom":[subQ3,subQ1]});Q61=makeQuery(id+"F0.imprint","IMPRINT",FACE,{"disambiguationData":[TD([[makeQuery(id+"F0.imprint","IMPRINT",EDGE,{"disambiguationData":[TD([[subQ4,-1.0]])],"derivedFrom":subQ3}),-1.0]])]});}
            var Q62;
            {var subQ1=sQuery(id+"F0.wireOp",EDGE,"E51.3");var subQ7=sQuery(id+"F0.wireOp",EDGE,"E5");var subQ8=makeQuery(id+"F0.imprint","INTERSECT",VERTEX,{"derivedFrom":[subQ7,subQ1]});Q62=makeQuery(id+"F0.imprint","IMPRINT",FACE,{"disambiguationData":[TD([[makeQuery(id+"F0.imprint","IMPRINT",EDGE,{"disambiguationData":[TD([[subQ8,-1.0]])],"derivedFrom":subQ7}),1.0]])]});}
            var Q63;
            {var subQ0=sQuery(id+"F0.wireOp",EDGE,"E51.4");var subQ1=sQuery(id+"F0.wireOp",EDGE,"E6");var subQ2=makeQuery(id+"F0.imprint","INTERSECT",VERTEX,{"derivedFrom":[subQ1,subQ0]});Q63=makeQuery(id+"F0.imprint","IMPRINT",FACE,{"disambiguationData":[TD([[makeQuery(id+"F0.imprint","IMPRINT",EDGE,{"disambiguationData":[TD([[subQ2,-1.0]])],"derivedFrom":subQ1}),1.0]])]});}
            var Q64;
            {var subQ0=sQuery(id+"F0.wireOp",EDGE,"E51.4");var subQ1=sQuery(id+"F0.wireOp",EDGE,"E20");var subQ2=makeQuery(id+"F0.imprint","INTERSECT",VERTEX,{"derivedFrom":[subQ1,subQ0]});Q64=makeQuery(id+"F0.imprint","IMPRINT",FACE,{"disambiguationData":[TD([[makeQuery(id+"F0.imprint","IMPRINT",EDGE,{"disambiguationData":[TD([[subQ2,-1.0]])],"derivedFrom":subQ1}),-1.0]])]});}
            var Q65;
            {var subQ0=sQuery(id+"F0.wireOp",EDGE,"E52.5");var subQ1=sQuery(id+"F0.wireOp",EDGE,"E7");var subQ2=makeQuery(id+"F0.imprint","INTERSECT",VERTEX,{"derivedFrom":[subQ1,subQ0]});Q65=makeQuery(id+"F0.imprint","IMPRINT",FACE,{"disambiguationData":[TD([[makeQuery(id+"F0.imprint","IMPRINT",EDGE,{"disambiguationData":[TD([[subQ2,-1.0]])],"derivedFrom":subQ1}),1.0]])]});}
            var Q66;
            {var subQ0=sQuery(id+"F0.wireOp",EDGE,"E51.6");var subQ1=sQuery(id+"F0.wireOp",EDGE,"E14");var subQ2=makeQuery(id+"F0.imprint","INTERSECT",VERTEX,{"derivedFrom":[subQ1,subQ0]});Q66=makeQuery(id+"F0.imprint","IMPRINT",FACE,{"disambiguationData":[TD([[makeQuery(id+"F0.imprint","IMPRINT",EDGE,{"disambiguationData":[TD([[subQ2,-1.0]])],"derivedFrom":subQ1}),1.0]])]});}
            var Q67;
            {var subQ1=sQuery(id+"F0.wireOp",EDGE,"E51.6");var subQ8=sQuery(id+"F0.wireOp",EDGE,"E36");var subQ10=makeQuery(id+"F0.imprint","INTERSECT",VERTEX,{"derivedFrom":[subQ8,subQ1]});Q67=makeQuery(id+"F0.imprint","IMPRINT",FACE,{"disambiguationData":[TD([[makeQuery(id+"F0.imprint","IMPRINT",EDGE,{"disambiguationData":[TD([[subQ10,-1.0]])],"derivedFrom":subQ8}),1.0]])]});}
            var Q68;
            {var subQ0=sQuery(id+"F0.wireOp",EDGE,"E51.7");var subQ1=sQuery(id+"F0.wireOp",EDGE,"E38");var subQ2=makeQuery(id+"F0.imprint","INTERSECT",VERTEX,{"derivedFrom":[subQ1,subQ0]});Q68=makeQuery(id+"F0.imprint","IMPRINT",FACE,{"disambiguationData":[TD([[makeQuery(id+"F0.imprint","IMPRINT",EDGE,{"disambiguationData":[TD([[subQ2,-1.0]])],"derivedFrom":subQ1}),1.0]])]});}
            var Q69;
            {var subQ0=sQuery(id+"F0.wireOp",EDGE,"E51.7");var subQ1=sQuery(id+"F0.wireOp",EDGE,"E40");var subQ2=makeQuery(id+"F0.imprint","INTERSECT",VERTEX,{"derivedFrom":[subQ1,subQ0]});Q69=makeQuery(id+"F0.imprint","IMPRINT",FACE,{"disambiguationData":[TD([[makeQuery(id+"F0.imprint","IMPRINT",EDGE,{"disambiguationData":[TD([[subQ2,-1.0]])],"derivedFrom":subQ1}),1.0]])]});}
            var Q70;
            {var subQ0=sQuery(id+"F0.wireOp",EDGE,"E51.7");var subQ3=sQuery(id+"F0.wireOp",EDGE,"E42");var subQ4=makeQuery(id+"F0.imprint","INTERSECT",VERTEX,{"derivedFrom":[subQ3,subQ0]});Q70=makeQuery(id+"F0.imprint","IMPRINT",FACE,{"disambiguationData":[TD([[makeQuery(id+"F0.imprint","IMPRINT",EDGE,{"disambiguationData":[TD([[subQ4,-1.0]])],"derivedFrom":subQ3}),1.0]])]});}
            var Q71;
            {var subQ0=sQuery(id+"F0.wireOp",EDGE,"E51.0");var subQ1=sQuery(id+"F0.wireOp",EDGE,"E34");var subQ2=makeQuery(id+"F0.imprint","INTERSECT",VERTEX,{"derivedFrom":[subQ1,subQ0]});Q71=makeQuery(id+"F0.imprint","IMPRINT",FACE,{"disambiguationData":[TD([[makeQuery(id+"F0.imprint","IMPRINT",EDGE,{"disambiguationData":[TD([[subQ2,-1.0]])],"derivedFrom":subQ1}),-1.0]])]});}
            var Q72;
            {var subQ0=sQuery(id+"F0.wireOp",EDGE,"E51.1");var subQ3=sQuery(id+"F0.wireOp",EDGE,"E30");var subQ4=makeQuery(id+"F0.imprint","INTERSECT",VERTEX,{"derivedFrom":[subQ3,subQ0]});Q72=makeQuery(id+"F0.imprint","IMPRINT",FACE,{"disambiguationData":[TD([[makeQuery(id+"F0.imprint","IMPRINT",EDGE,{"disambiguationData":[TD([[subQ4,-1.0]])],"derivedFrom":subQ3}),-1.0]])]});}
            var Q73;
            {var subQ0=sQuery(id+"F0.wireOp",EDGE,"E51.1");var subQ1=sQuery(id+"F0.wireOp",EDGE,"E28");var subQ2=makeQuery(id+"F0.imprint","INTERSECT",VERTEX,{"derivedFrom":[subQ1,subQ0]});Q73=makeQuery(id+"F0.imprint","IMPRINT",FACE,{"disambiguationData":[TD([[makeQuery(id+"F0.imprint","IMPRINT",EDGE,{"disambiguationData":[TD([[subQ2,-1.0]])],"derivedFrom":subQ1}),-1.0]])]});}
            var Q74;
            {var subQ0=sQuery(id+"F0.wireOp",EDGE,"E51.1");var subQ1=sQuery(id+"F0.wireOp",EDGE,"E26");var subQ2=makeQuery(id+"F0.imprint","INTERSECT",VERTEX,{"derivedFrom":[subQ1,subQ0]});Q74=makeQuery(id+"F0.imprint","IMPRINT",FACE,{"disambiguationData":[TD([[makeQuery(id+"F0.imprint","IMPRINT",EDGE,{"disambiguationData":[TD([[subQ2,-1.0]])],"derivedFrom":subQ1}),-1.0]])]});}
            var Q75;
            {var subQ0=sQuery(id+"F0.wireOp",EDGE,"E51.1");var subQ1=sQuery(id+"F0.wireOp",EDGE,"E24");var subQ2=makeQuery(id+"F0.imprint","INTERSECT",VERTEX,{"derivedFrom":[subQ1,subQ0]});Q75=makeQuery(id+"F0.imprint","IMPRINT",FACE,{"disambiguationData":[TD([[makeQuery(id+"F0.imprint","IMPRINT",EDGE,{"disambiguationData":[TD([[subQ2,-1.0]])],"derivedFrom":subQ1}),-1.0]])]});}
            var Q76;
            {var subQ0=sQuery(id+"F0.wireOp",EDGE,"E51.2");var subQ3=sQuery(id+"F0.wireOp",EDGE,"E22");var subQ4=makeQuery(id+"F0.imprint","INTERSECT",VERTEX,{"derivedFrom":[subQ3,subQ0]});Q76=makeQuery(id+"F0.imprint","IMPRINT",FACE,{"disambiguationData":[TD([[makeQuery(id+"F0.imprint","IMPRINT",EDGE,{"disambiguationData":[TD([[subQ4,-1.0]])],"derivedFrom":subQ3}),-1.0]])]});}
            var Q77;
            {var subQ0=sQuery(id+"F0.wireOp",EDGE,"E51.2");var subQ1=sQuery(id+"F0.wireOp",EDGE,"E19");var subQ2=makeQuery(id+"F0.imprint","INTERSECT",VERTEX,{"derivedFrom":[subQ1,subQ0]});Q77=makeQuery(id+"F0.imprint","IMPRINT",FACE,{"disambiguationData":[TD([[makeQuery(id+"F0.imprint","IMPRINT",EDGE,{"disambiguationData":[TD([[subQ2,-1.0]])],"derivedFrom":subQ1}),-1.0]])]});}
            var Q78;
            {var subQ0=sQuery(id+"F0.wireOp",EDGE,"E51.2");var subQ1=sQuery(id+"F0.wireOp",EDGE,"E19");var subQ2=makeQuery(id+"F0.imprint","INTERSECT",VERTEX,{"derivedFrom":[subQ1,subQ0]});Q78=makeQuery(id+"F0.imprint","IMPRINT",FACE,{"disambiguationData":[TD([[makeQuery(id+"F0.imprint","IMPRINT",EDGE,{"disambiguationData":[TD([[subQ2,-1.0]])],"derivedFrom":subQ1}),1.0]])]});}
            var Q79;
            {var subQ0=sQuery(id+"F0.wireOp",EDGE,"E51.2");var subQ1=sQuery(id+"F0.wireOp",EDGE,"E18");var subQ2=makeQuery(id+"F0.imprint","INTERSECT",VERTEX,{"derivedFrom":[subQ1,subQ0]});Q79=makeQuery(id+"F0.imprint","IMPRINT",FACE,{"disambiguationData":[TD([[makeQuery(id+"F0.imprint","IMPRINT",EDGE,{"disambiguationData":[TD([[subQ2,-1.0]])],"derivedFrom":subQ1}),-1.0]])]});}
            var Q80;
            {var subQ5=sQuery(id+"F0.wireOp",EDGE,"E51.3");var subQ7=sQuery(id+"F0.wireOp",EDGE,"E17");var subQ8=makeQuery(id+"F0.imprint","INTERSECT",VERTEX,{"derivedFrom":[subQ7,subQ5]});Q80=makeQuery(id+"F0.imprint","IMPRINT",FACE,{"disambiguationData":[TD([[makeQuery(id+"F0.imprint","IMPRINT",EDGE,{"disambiguationData":[TD([[subQ8,-1.0]])],"derivedFrom":subQ7}),-1.0]])]});}
            var Q81;
            {var subQ0=sQuery(id+"F0.wireOp",EDGE,"E52.4");var subQ1=sQuery(id+"F0.wireOp",EDGE,"E15");var subQ2=makeQuery(id+"F0.imprint","INTERSECT",VERTEX,{"derivedFrom":[subQ1,subQ0]});Q81=makeQuery(id+"F0.imprint","IMPRINT",FACE,{"disambiguationData":[TD([[makeQuery(id+"F0.imprint","IMPRINT",EDGE,{"disambiguationData":[TD([[subQ2,-1.0]])],"derivedFrom":subQ1}),1.0]])]});}
            var Q82;
            {var subQ5=sQuery(id+"F0.wireOp",EDGE,"E52.5");var subQ6=sQuery(id+"F0.wireOp",EDGE,"E7");var subQ7=makeQuery(id+"F0.imprint","INTERSECT",VERTEX,{"derivedFrom":[subQ6,subQ5]});Q82=makeQuery(id+"F0.imprint","IMPRINT",FACE,{"disambiguationData":[TD([[makeQuery(id+"F0.imprint","IMPRINT",EDGE,{"disambiguationData":[TD([[subQ7,-1.0]])],"derivedFrom":subQ6}),-1.0]])]});}
            var Q83;
            {var subQ0=sQuery(id+"F0.wireOp",EDGE,"E51.5");var subQ1=sQuery(id+"F0.wireOp",EDGE,"E9");var subQ2=makeQuery(id+"F0.imprint","INTERSECT",VERTEX,{"derivedFrom":[subQ1,subQ0]});Q83=makeQuery(id+"F0.imprint","IMPRINT",FACE,{"disambiguationData":[TD([[makeQuery(id+"F0.imprint","IMPRINT",EDGE,{"disambiguationData":[TD([[subQ2,-1.0]])],"derivedFrom":subQ1}),1.0]])]});}
            var Q84;
            {var subQ0=sQuery(id+"F0.wireOp",EDGE,"E51.5");var subQ1=sQuery(id+"F0.wireOp",EDGE,"E11");var subQ2=makeQuery(id+"F0.imprint","INTERSECT",VERTEX,{"derivedFrom":[subQ1,subQ0]});Q84=makeQuery(id+"F0.imprint","IMPRINT",FACE,{"disambiguationData":[TD([[makeQuery(id+"F0.imprint","IMPRINT",EDGE,{"disambiguationData":[TD([[subQ2,-1.0]])],"derivedFrom":subQ1}),1.0]])]});}
            var Q85;
            {var subQ3=sQuery(id+"F0.wireOp",EDGE,"E12");var subQ9=sQuery(id+"F0.wireOp",EDGE,"E52.6");var subQ10=makeQuery(id+"F0.imprint","INTERSECT",VERTEX,{"derivedFrom":[subQ3,subQ9]});Q85=makeQuery(id+"F0.imprint","IMPRINT",FACE,{"disambiguationData":[TD([[makeQuery(id+"F0.imprint","IMPRINT",EDGE,{"disambiguationData":[TD([[subQ10,-1.0]])],"derivedFrom":subQ3}),-1.0]])]});}
            var Q86;
            {var subQ0=sQuery(id+"F0.wireOp",EDGE,"E52.7");var subQ1=sQuery(id+"F0.wireOp",EDGE,"E35");var subQ2=makeQuery(id+"F0.imprint","INTERSECT",VERTEX,{"derivedFrom":[subQ1,subQ0]});Q86=makeQuery(id+"F0.imprint","IMPRINT",FACE,{"disambiguationData":[TD([[makeQuery(id+"F0.imprint","IMPRINT",EDGE,{"disambiguationData":[TD([[subQ2,-1.0]])],"derivedFrom":subQ1}),1.0]])]});}
            var Q87;
            {var subQ0=sQuery(id+"F0.wireOp",EDGE,"E52.0");var subQ1=sQuery(id+"F0.wireOp",EDGE,"E39");var subQ2=makeQuery(id+"F0.imprint","INTERSECT",VERTEX,{"derivedFrom":[subQ1,subQ0]});Q87=makeQuery(id+"F0.imprint","IMPRINT",FACE,{"disambiguationData":[TD([[makeQuery(id+"F0.imprint","IMPRINT",EDGE,{"disambiguationData":[TD([[subQ2,-1.0]])],"derivedFrom":subQ1}),1.0]])]});}
            var Q88;
            {var subQ0=sQuery(id+"F0.wireOp",EDGE,"E51.0");var subQ1=sQuery(id+"F0.wireOp",EDGE,"E44");var subQ2=makeQuery(id+"F0.imprint","INTERSECT",VERTEX,{"derivedFrom":[subQ1,subQ0]});Q88=makeQuery(id+"F0.imprint","IMPRINT",FACE,{"disambiguationData":[TD([[makeQuery(id+"F0.imprint","IMPRINT",EDGE,{"disambiguationData":[TD([[subQ2,-1.0]])],"derivedFrom":subQ1}),1.0]])]});}
            var Q89;
            {var subQ0=sQuery(id+"F0.wireOp",EDGE,"E52.1");var subQ1=sQuery(id+"F0.wireOp",EDGE,"E31");var subQ2=makeQuery(id+"F0.imprint","INTERSECT",VERTEX,{"derivedFrom":[subQ1,subQ0]});Q89=makeQuery(id+"F0.imprint","IMPRINT",FACE,{"disambiguationData":[TD([[makeQuery(id+"F0.imprint","IMPRINT",EDGE,{"disambiguationData":[TD([[subQ2,-1.0]])],"derivedFrom":subQ1}),1.0]])]});}
            var Q90;
            {var subQ13=sQuery(id+"F0.wireOp",EDGE,"E4");Q90=makeQuery(id+"F0.imprint","IMPRINT",FACE,{"disambiguationData":[TD([[makeQuery(id+"F0.imprint","IMPRINT",EDGE,{"derivedFrom":subQ13}),1.0]])]});}
            var Q91;
            {var subQ0=sQuery(id+"F0.wireOp",EDGE,"E4");Q91=makeQuery(id+"F0.imprint","IMPRINT",FACE,{"disambiguationData":[TD([[makeQuery(id+"F0.imprint","IMPRINT",EDGE,{"derivedFrom":subQ0}),-1.0]])]});}
            var Q92;
            {var subQ10=sQuery(id+"F0.wireOp",EDGE,"E8");Q92=makeQuery(id+"F0.imprint","IMPRINT",FACE,{"disambiguationData":[TD([[makeQuery(id+"F0.imprint","IMPRINT",EDGE,{"derivedFrom":subQ10}),1.0]])]});}
            var Q93;
            {var subQ6=sQuery(id+"F0.wireOp",EDGE,"E8");Q93=makeQuery(id+"F0.imprint","IMPRINT",FACE,{"disambiguationData":[TD([[makeQuery(id+"F0.imprint","IMPRINT",EDGE,{"derivedFrom":subQ6}),-1.0]])]});}
            var Q94;
            {var subQ33=sQuery(id+"F0.wireOp",EDGE,"E13");Q94=makeQuery(id+"F0.imprint","IMPRINT",FACE,{"disambiguationData":[TD([[makeQuery(id+"F0.imprint","IMPRINT",EDGE,{"derivedFrom":subQ33}),1.0]])]});}
            var Q95;
            {var subQ5=sQuery(id+"F0.wireOp",EDGE,"E13");Q95=makeQuery(id+"F0.imprint","IMPRINT",FACE,{"disambiguationData":[TD([[makeQuery(id+"F0.imprint","IMPRINT",EDGE,{"derivedFrom":subQ5}),-1.0]])]});}
            var Q96;
            {var subQ16=sQuery(id+"F0.wireOp",EDGE,"E2.2");var subQ17=sQuery(id+"F0.wireOp",EDGE,"E1");var subQ18=makeQuery(id+"F0.imprint","INTERSECT",VERTEX,{"disambiguationData":[OD(1.0)],"derivedFrom":[subQ17,subQ16]});Q96=makeQuery(id+"F0.imprint","IMPRINT",FACE,{"disambiguationData":[TD([[makeQuery(id+"F0.imprint","IMPRINT",EDGE,{"disambiguationData":[TD([[subQ18,-1.0]])],"derivedFrom":subQ17}),1.0]])]});}
            var Q97;
            {var subQ1=sQuery(id+"F0.wireOp",EDGE,"E2.1");var subQ3=sQuery(id+"F0.wireOp",EDGE,"E46");var subQ4=makeQuery(id+"F0.imprint","INTERSECT",VERTEX,{"derivedFrom":[subQ1,subQ3]});Q97=makeQuery(id+"F0.imprint","IMPRINT",FACE,{"disambiguationData":[TD([[makeQuery(id+"F0.imprint","IMPRINT",EDGE,{"disambiguationData":[TD([[subQ4,-1.0]])],"derivedFrom":subQ3}),1.0]])]});}
            var Q98;
            {var subQ6=sQuery(id+"F0.wireOp",EDGE,"E1");var subQ11=sQuery(id+"F0.wireOp",EDGE,"E2.3");var subQ12=makeQuery(id+"F0.imprint","INTERSECT",VERTEX,{"disambiguationData":[OD(1.0)],"derivedFrom":[subQ6,subQ11]});Q98=makeQuery(id+"F0.imprint","IMPRINT",FACE,{"disambiguationData":[TD([[makeQuery(id+"F0.imprint","IMPRINT",EDGE,{"disambiguationData":[TD([[subQ12,-1.0]])],"derivedFrom":subQ6}),1.0]])]});}
            var Q99;
            {var subQ0=sQuery(id+"F0.wireOp",EDGE,"E16");Q99=makeQuery(id+"F0.imprint","IMPRINT",FACE,{"disambiguationData":[TD([[makeQuery(id+"F0.imprint","IMPRINT",EDGE,{"derivedFrom":subQ0}),1.0]])]});}
            extrude(context, id + "F1", {"entities" : qUnion([Q0, Q1, Q2, Q3, Q4, Q5, Q6, Q7, Q8, Q9, Q10, Q11, Q12, Q13, Q14, Q15, Q16, Q17, Q18, Q19, Q20, Q21, Q22, Q23, Q24, Q25, Q26, Q27, Q28, Q29, Q30, Q31, Q32, Q33, Q34, Q35, Q36, Q37, Q38, Q39, Q40, Q41, Q42, Q43, Q44, Q45, Q46, Q47, Q48, Q49, Q50, Q51, Q52, Q53, Q54, Q55, Q56, Q57, Q58, Q59, Q60, Q61, Q62, Q63, Q64, Q65, Q66, Q67, Q68, Q69, Q70, Q71, Q72, Q73, Q74, Q75, Q76, Q77, Q78, Q79, Q80, Q81, Q82, Q83, Q84, Q85, Q86, Q87, Q88, Q89, Q90, Q91, Q92, Q93, Q94, Q95, Q96, Q97, Q98, Q99]), "depth" : 25.4 * mm});
        }
        {
            var Q0;
            Q0=makeQuery(id+"F0.imprint","IMPRINT",FACE,{"disambiguationData":[TD([[makeQuery(id+"F0.imprint","IMPRINT",EDGE,{"derivedFrom":sQuery(id+"F0.wireOp",EDGE,"E0")}),1.0]])]});
            var Q1;
            {var subQ3=sQuery(id+"F0.wireOp",EDGE,"E42");var subQ5=sQuery(id+"F0.wireOp",EDGE,"E53.0");var subQ6=makeQuery(id+"F0.imprint","INTERSECT",VERTEX,{"derivedFrom":[subQ3,subQ5]});Q1=makeQuery(id+"F0.imprint","IMPRINT",FACE,{"disambiguationData":[TD([[makeQuery(id+"F0.imprint","IMPRINT",EDGE,{"disambiguationData":[TD([[subQ6,-1.0]])],"derivedFrom":subQ3}),1.0]])]});}
            var Q2;
            {var subQ0=sQuery(id+"F0.wireOp",EDGE,"E53.0");var subQ1=sQuery(id+"F0.wireOp",EDGE,"E40");var subQ2=makeQuery(id+"F0.imprint","INTERSECT",VERTEX,{"derivedFrom":[subQ1,subQ0]});Q2=makeQuery(id+"F0.imprint","IMPRINT",FACE,{"disambiguationData":[TD([[makeQuery(id+"F0.imprint","IMPRINT",EDGE,{"disambiguationData":[TD([[subQ2,-1.0]])],"derivedFrom":subQ1}),1.0]])]});}
            var Q3;
            {var subQ0=sQuery(id+"F0.wireOp",EDGE,"E54.0");var subQ1=sQuery(id+"F0.wireOp",EDGE,"E39");var subQ2=makeQuery(id+"F0.imprint","INTERSECT",VERTEX,{"derivedFrom":[subQ1,subQ0]});Q3=makeQuery(id+"F0.imprint","IMPRINT",FACE,{"disambiguationData":[TD([[makeQuery(id+"F0.imprint","IMPRINT",EDGE,{"disambiguationData":[TD([[subQ2,-1.0]])],"derivedFrom":subQ1}),1.0]])]});}
            var Q4;
            {var subQ0=sQuery(id+"F0.wireOp",EDGE,"E53.7");var subQ3=sQuery(id+"F0.wireOp",EDGE,"E38");var subQ4=makeQuery(id+"F0.imprint","INTERSECT",VERTEX,{"derivedFrom":[subQ3,subQ0]});Q4=makeQuery(id+"F0.imprint","IMPRINT",FACE,{"disambiguationData":[TD([[makeQuery(id+"F0.imprint","IMPRINT",EDGE,{"disambiguationData":[TD([[subQ4,-1.0]])],"derivedFrom":subQ3}),1.0]])]});}
            var Q5;
            {var subQ0=sQuery(id+"F0.wireOp",EDGE,"E53.7");var subQ1=sQuery(id+"F0.wireOp",EDGE,"E36");var subQ2=makeQuery(id+"F0.imprint","INTERSECT",VERTEX,{"derivedFrom":[subQ1,subQ0]});Q5=makeQuery(id+"F0.imprint","IMPRINT",FACE,{"disambiguationData":[TD([[makeQuery(id+"F0.imprint","IMPRINT",EDGE,{"disambiguationData":[TD([[subQ2,-1.0]])],"derivedFrom":subQ1}),1.0]])]});}
            var Q6;
            {var subQ1=sQuery(id+"F0.wireOp",EDGE,"E54.0");var subQ3=sQuery(id+"F0.wireOp",EDGE,"E35");var subQ4=makeQuery(id+"F0.imprint","INTERSECT",VERTEX,{"derivedFrom":[subQ3,subQ1]});Q6=makeQuery(id+"F0.imprint","IMPRINT",FACE,{"disambiguationData":[TD([[makeQuery(id+"F0.imprint","IMPRINT",EDGE,{"disambiguationData":[TD([[subQ4,-1.0]])],"derivedFrom":subQ3}),1.0]])]});}
            var Q7;
            {var subQ0=sQuery(id+"F0.wireOp",EDGE,"E54.5");var subQ1=sQuery(id+"F0.wireOp",EDGE,"E12");var subQ2=makeQuery(id+"F0.imprint","INTERSECT",VERTEX,{"derivedFrom":[subQ1,subQ0]});Q7=makeQuery(id+"F0.imprint","IMPRINT",FACE,{"disambiguationData":[TD([[makeQuery(id+"F0.imprint","IMPRINT",EDGE,{"disambiguationData":[TD([[subQ2,-1.0]])],"derivedFrom":subQ1}),-1.0]])]});}
            var Q8;
            {var subQ1=sQuery(id+"F0.wireOp",EDGE,"E53.6");var subQ3=sQuery(id+"F0.wireOp",EDGE,"E14");var subQ4=makeQuery(id+"F0.imprint","INTERSECT",VERTEX,{"derivedFrom":[subQ3,subQ1]});Q8=makeQuery(id+"F0.imprint","IMPRINT",FACE,{"disambiguationData":[TD([[makeQuery(id+"F0.imprint","IMPRINT",EDGE,{"disambiguationData":[TD([[subQ4,-1.0]])],"derivedFrom":subQ3}),1.0]])]});}
            var Q9;
            {var subQ0=sQuery(id+"F0.wireOp",EDGE,"E53.6");var subQ1=sQuery(id+"F0.wireOp",EDGE,"E11");var subQ2=makeQuery(id+"F0.imprint","INTERSECT",VERTEX,{"derivedFrom":[subQ1,subQ0]});Q9=makeQuery(id+"F0.imprint","IMPRINT",FACE,{"disambiguationData":[TD([[makeQuery(id+"F0.imprint","IMPRINT",EDGE,{"disambiguationData":[TD([[subQ2,-1.0]])],"derivedFrom":subQ1}),1.0]])]});}
            var Q10;
            {var subQ1=sQuery(id+"F0.wireOp",EDGE,"E53.5");var subQ5=sQuery(id+"F0.wireOp",EDGE,"E9");var subQ6=makeQuery(id+"F0.imprint","INTERSECT",VERTEX,{"derivedFrom":[subQ5,subQ1]});Q10=makeQuery(id+"F0.imprint","IMPRINT",FACE,{"disambiguationData":[TD([[makeQuery(id+"F0.imprint","IMPRINT",EDGE,{"disambiguationData":[TD([[subQ6,-1.0]])],"derivedFrom":subQ5}),1.0]])]});}
            var Q11;
            {var subQ0=sQuery(id+"F0.wireOp",EDGE,"E54.4");var subQ1=sQuery(id+"F0.wireOp",EDGE,"E7");var subQ2=makeQuery(id+"F0.imprint","INTERSECT",VERTEX,{"derivedFrom":[subQ1,subQ0]});Q11=makeQuery(id+"F0.imprint","IMPRINT",FACE,{"disambiguationData":[TD([[makeQuery(id+"F0.imprint","IMPRINT",EDGE,{"disambiguationData":[TD([[subQ2,-1.0]])],"derivedFrom":subQ1}),-1.0]])]});}
            var Q12;
            {var subQ0=sQuery(id+"F0.wireOp",EDGE,"E54.4");var subQ1=sQuery(id+"F0.wireOp",EDGE,"E7");var subQ2=makeQuery(id+"F0.imprint","INTERSECT",VERTEX,{"derivedFrom":[subQ1,subQ0]});Q12=makeQuery(id+"F0.imprint","IMPRINT",FACE,{"disambiguationData":[TD([[makeQuery(id+"F0.imprint","IMPRINT",EDGE,{"disambiguationData":[TD([[subQ2,-1.0]])],"derivedFrom":subQ1}),1.0]])]});}
            var Q13;
            {var subQ0=sQuery(id+"F0.wireOp",EDGE,"E53.5");var subQ1=sQuery(id+"F0.wireOp",EDGE,"E6");var subQ2=makeQuery(id+"F0.imprint","INTERSECT",VERTEX,{"derivedFrom":[subQ1,subQ0]});Q13=makeQuery(id+"F0.imprint","IMPRINT",FACE,{"disambiguationData":[TD([[makeQuery(id+"F0.imprint","IMPRINT",EDGE,{"disambiguationData":[TD([[subQ2,-1.0]])],"derivedFrom":subQ1}),1.0]])]});}
            var Q14;
            {var subQ1=sQuery(id+"F0.wireOp",EDGE,"E53.4");var subQ7=sQuery(id+"F0.wireOp",EDGE,"E5");var subQ8=makeQuery(id+"F0.imprint","INTERSECT",VERTEX,{"derivedFrom":[subQ7,subQ1]});Q14=makeQuery(id+"F0.imprint","IMPRINT",FACE,{"disambiguationData":[TD([[makeQuery(id+"F0.imprint","IMPRINT",EDGE,{"disambiguationData":[TD([[subQ8,-1.0]])],"derivedFrom":subQ7}),1.0]])]});}
            var Q15;
            {var subQ0=sQuery(id+"F0.wireOp",EDGE,"E54.3");var subQ1=sQuery(id+"F0.wireOp",EDGE,"E3");var subQ2=makeQuery(id+"F0.imprint","INTERSECT",VERTEX,{"derivedFrom":[subQ1,subQ0]});Q15=makeQuery(id+"F0.imprint","IMPRINT",FACE,{"disambiguationData":[TD([[makeQuery(id+"F0.imprint","IMPRINT",EDGE,{"disambiguationData":[TD([[subQ2,-1.0]])],"derivedFrom":subQ1}),-1.0]])]});}
            var Q16;
            {var subQ0=sQuery(id+"F0.wireOp",EDGE,"E54.3");var subQ1=sQuery(id+"F0.wireOp",EDGE,"E3");var subQ2=makeQuery(id+"F0.imprint","INTERSECT",VERTEX,{"derivedFrom":[subQ1,subQ0]});Q16=makeQuery(id+"F0.imprint","IMPRINT",FACE,{"disambiguationData":[TD([[makeQuery(id+"F0.imprint","IMPRINT",EDGE,{"disambiguationData":[TD([[subQ2,-1.0]])],"derivedFrom":subQ1}),1.0]])]});}
            var Q17;
            {var subQ0=sQuery(id+"F0.wireOp",EDGE,"E53.3");var subQ1=sQuery(id+"F0.wireOp",EDGE,"E17");var subQ2=makeQuery(id+"F0.imprint","INTERSECT",VERTEX,{"derivedFrom":[subQ1,subQ0]});Q17=makeQuery(id+"F0.imprint","IMPRINT",FACE,{"disambiguationData":[TD([[makeQuery(id+"F0.imprint","IMPRINT",EDGE,{"disambiguationData":[TD([[subQ2,-1.0]])],"derivedFrom":subQ1}),-1.0]])]});}
            var Q18;
            {var subQ0=sQuery(id+"F0.wireOp",EDGE,"E53.3");var subQ3=sQuery(id+"F0.wireOp",EDGE,"E19");var subQ4=makeQuery(id+"F0.imprint","INTERSECT",VERTEX,{"derivedFrom":[subQ3,subQ0]});Q18=makeQuery(id+"F0.imprint","IMPRINT",FACE,{"disambiguationData":[TD([[makeQuery(id+"F0.imprint","IMPRINT",EDGE,{"disambiguationData":[TD([[subQ4,-1.0]])],"derivedFrom":subQ3}),-1.0]])]});}
            var Q19;
            {var subQ0=sQuery(id+"F0.wireOp",EDGE,"E53.2");var subQ1=sQuery(id+"F0.wireOp",EDGE,"E22");var subQ2=makeQuery(id+"F0.imprint","INTERSECT",VERTEX,{"derivedFrom":[subQ1,subQ0]});Q19=makeQuery(id+"F0.imprint","IMPRINT",FACE,{"disambiguationData":[TD([[makeQuery(id+"F0.imprint","IMPRINT",EDGE,{"disambiguationData":[TD([[subQ2,-1.0]])],"derivedFrom":subQ1}),-1.0]])]});}
            var Q20;
            {var subQ0=sQuery(id+"F0.wireOp",EDGE,"E53.2");var subQ1=sQuery(id+"F0.wireOp",EDGE,"E24");var subQ2=makeQuery(id+"F0.imprint","INTERSECT",VERTEX,{"derivedFrom":[subQ1,subQ0]});Q20=makeQuery(id+"F0.imprint","IMPRINT",FACE,{"disambiguationData":[TD([[makeQuery(id+"F0.imprint","IMPRINT",EDGE,{"disambiguationData":[TD([[subQ2,-1.0]])],"derivedFrom":subQ1}),-1.0]])]});}
            var Q21;
            {var subQ0=sQuery(id+"F0.wireOp",EDGE,"E53.2");var subQ1=sQuery(id+"F0.wireOp",EDGE,"E26");var subQ2=makeQuery(id+"F0.imprint","INTERSECT",VERTEX,{"derivedFrom":[subQ1,subQ0]});Q21=makeQuery(id+"F0.imprint","IMPRINT",FACE,{"disambiguationData":[TD([[makeQuery(id+"F0.imprint","IMPRINT",EDGE,{"disambiguationData":[TD([[subQ2,-1.0]])],"derivedFrom":subQ1}),-1.0]])]});}
            var Q22;
            {var subQ0=sQuery(id+"F0.wireOp",EDGE,"E53.3");var subQ1=sQuery(id+"F0.wireOp",EDGE,"E19");var subQ2=makeQuery(id+"F0.imprint","INTERSECT",VERTEX,{"derivedFrom":[subQ1,subQ0]});Q22=makeQuery(id+"F0.imprint","IMPRINT",FACE,{"disambiguationData":[TD([[makeQuery(id+"F0.imprint","IMPRINT",EDGE,{"disambiguationData":[TD([[subQ2,-1.0]])],"derivedFrom":subQ1}),1.0]])]});}
            var Q23;
            {var subQ1=sQuery(id+"F0.wireOp",EDGE,"E53.1");var subQ5=sQuery(id+"F0.wireOp",EDGE,"E30");var subQ6=makeQuery(id+"F0.imprint","INTERSECT",VERTEX,{"derivedFrom":[subQ5,subQ1]});Q23=makeQuery(id+"F0.imprint","IMPRINT",FACE,{"disambiguationData":[TD([[makeQuery(id+"F0.imprint","IMPRINT",EDGE,{"disambiguationData":[TD([[subQ6,-1.0]])],"derivedFrom":subQ5}),1.0]])]});}
            var Q24;
            {var subQ0=sQuery(id+"F0.wireOp",EDGE,"E53.1");var subQ1=sQuery(id+"F0.wireOp",EDGE,"E30");var subQ2=makeQuery(id+"F0.imprint","INTERSECT",VERTEX,{"derivedFrom":[subQ1,subQ0]});Q24=makeQuery(id+"F0.imprint","IMPRINT",FACE,{"disambiguationData":[TD([[makeQuery(id+"F0.imprint","IMPRINT",EDGE,{"disambiguationData":[TD([[subQ2,-1.0]])],"derivedFrom":subQ1}),-1.0]])]});}
            var Q25;
            {var subQ0=sQuery(id+"F0.wireOp",EDGE,"E54.1");var subQ1=sQuery(id+"F0.wireOp",EDGE,"E31");var subQ2=makeQuery(id+"F0.imprint","INTERSECT",VERTEX,{"derivedFrom":[subQ1,subQ0]});Q25=makeQuery(id+"F0.imprint","IMPRINT",FACE,{"disambiguationData":[TD([[makeQuery(id+"F0.imprint","IMPRINT",EDGE,{"disambiguationData":[TD([[subQ2,-1.0]])],"derivedFrom":subQ1}),1.0]])]});}
            var Q26;
            {var subQ0=sQuery(id+"F0.wireOp",EDGE,"E53.1");var subQ1=sQuery(id+"F0.wireOp",EDGE,"E34");var subQ2=makeQuery(id+"F0.imprint","INTERSECT",VERTEX,{"derivedFrom":[subQ1,subQ0]});Q26=makeQuery(id+"F0.imprint","IMPRINT",FACE,{"disambiguationData":[TD([[makeQuery(id+"F0.imprint","IMPRINT",EDGE,{"disambiguationData":[TD([[subQ2,-1.0]])],"derivedFrom":subQ1}),-1.0]])]});}
            var Q27;
            {var subQ1=sQuery(id+"F0.wireOp",EDGE,"E53.0");var subQ5=sQuery(id+"F0.wireOp",EDGE,"E44");var subQ6=makeQuery(id+"F0.imprint","INTERSECT",VERTEX,{"derivedFrom":[subQ5,subQ1]});Q27=makeQuery(id+"F0.imprint","IMPRINT",FACE,{"disambiguationData":[TD([[makeQuery(id+"F0.imprint","IMPRINT",EDGE,{"disambiguationData":[TD([[subQ6,-1.0]])],"derivedFrom":subQ5}),1.0]])]});}
            var Q28;
            {var subQ0=sQuery(id+"F0.wireOp",EDGE,"E53.5");var subQ1=sQuery(id+"F0.wireOp",EDGE,"E20");var subQ2=makeQuery(id+"F0.imprint","INTERSECT",VERTEX,{"derivedFrom":[subQ1,subQ0]});Q28=makeQuery(id+"F0.imprint","IMPRINT",FACE,{"disambiguationData":[TD([[makeQuery(id+"F0.imprint","IMPRINT",EDGE,{"disambiguationData":[TD([[subQ2,-1.0]])],"derivedFrom":subQ1}),-1.0]])]});}
            var Q29;
            {var subQ3=sQuery(id+"F0.wireOp",EDGE,"E15");var subQ7=sQuery(id+"F0.wireOp",EDGE,"E54.3");var subQ9=makeQuery(id+"F0.imprint","INTERSECT",VERTEX,{"derivedFrom":[subQ3,subQ7]});Q29=makeQuery(id+"F0.imprint","IMPRINT",FACE,{"disambiguationData":[TD([[makeQuery(id+"F0.imprint","IMPRINT",EDGE,{"disambiguationData":[TD([[subQ9,-1.0]])],"derivedFrom":subQ3}),1.0]])]});}
            var Q30;
            {var subQ5=sQuery(id+"F0.wireOp",EDGE,"E53.3");var subQ6=sQuery(id+"F0.wireOp",EDGE,"E18");var subQ7=makeQuery(id+"F0.imprint","INTERSECT",VERTEX,{"derivedFrom":[subQ6,subQ5]});Q30=makeQuery(id+"F0.imprint","IMPRINT",FACE,{"disambiguationData":[TD([[makeQuery(id+"F0.imprint","IMPRINT",EDGE,{"disambiguationData":[TD([[subQ7,-1.0]])],"derivedFrom":subQ6}),-1.0]])]});}
            var Q31;
            {var subQ0=sQuery(id+"F0.wireOp",EDGE,"E51.2");var subQ1=sQuery(id+"F0.wireOp",EDGE,"E19");var subQ2=makeQuery(id+"F0.imprint","INTERSECT",VERTEX,{"derivedFrom":[subQ1,subQ0]});Q31=makeQuery(id+"F0.imprint","IMPRINT",FACE,{"disambiguationData":[TD([[makeQuery(id+"F0.imprint","IMPRINT",EDGE,{"disambiguationData":[TD([[subQ2,-1.0]])],"derivedFrom":subQ1}),1.0]])]});}
            var Q32;
            {var subQ0=sQuery(id+"F0.wireOp",EDGE,"E51.2");var subQ1=sQuery(id+"F0.wireOp",EDGE,"E18");var subQ2=makeQuery(id+"F0.imprint","INTERSECT",VERTEX,{"derivedFrom":[subQ1,subQ0]});Q32=makeQuery(id+"F0.imprint","IMPRINT",FACE,{"disambiguationData":[TD([[makeQuery(id+"F0.imprint","IMPRINT",EDGE,{"disambiguationData":[TD([[subQ2,-1.0]])],"derivedFrom":subQ1}),-1.0]])]});}
            var Q33;
            {var subQ5=sQuery(id+"F0.wireOp",EDGE,"E51.3");var subQ7=sQuery(id+"F0.wireOp",EDGE,"E17");var subQ8=makeQuery(id+"F0.imprint","INTERSECT",VERTEX,{"derivedFrom":[subQ7,subQ5]});Q33=makeQuery(id+"F0.imprint","IMPRINT",FACE,{"disambiguationData":[TD([[makeQuery(id+"F0.imprint","IMPRINT",EDGE,{"disambiguationData":[TD([[subQ8,-1.0]])],"derivedFrom":subQ7}),-1.0]])]});}
            var Q34;
            {var subQ0=sQuery(id+"F0.wireOp",EDGE,"E52.4");var subQ1=sQuery(id+"F0.wireOp",EDGE,"E15");var subQ2=makeQuery(id+"F0.imprint","INTERSECT",VERTEX,{"derivedFrom":[subQ1,subQ0]});Q34=makeQuery(id+"F0.imprint","IMPRINT",FACE,{"disambiguationData":[TD([[makeQuery(id+"F0.imprint","IMPRINT",EDGE,{"disambiguationData":[TD([[subQ2,-1.0]])],"derivedFrom":subQ1}),1.0]])]});}
            var Q35;
            {var subQ0=sQuery(id+"F0.wireOp",EDGE,"E52.4");var subQ1=sQuery(id+"F0.wireOp",EDGE,"E3");var subQ2=makeQuery(id+"F0.imprint","INTERSECT",VERTEX,{"derivedFrom":[subQ1,subQ0]});Q35=makeQuery(id+"F0.imprint","IMPRINT",FACE,{"disambiguationData":[TD([[makeQuery(id+"F0.imprint","IMPRINT",EDGE,{"disambiguationData":[TD([[subQ2,-1.0]])],"derivedFrom":subQ1}),1.0]])]});}
            var Q36;
            {var subQ1=sQuery(id+"F0.wireOp",EDGE,"E52.4");var subQ3=sQuery(id+"F0.wireOp",EDGE,"E3");var subQ4=makeQuery(id+"F0.imprint","INTERSECT",VERTEX,{"derivedFrom":[subQ3,subQ1]});Q36=makeQuery(id+"F0.imprint","IMPRINT",FACE,{"disambiguationData":[TD([[makeQuery(id+"F0.imprint","IMPRINT",EDGE,{"disambiguationData":[TD([[subQ4,-1.0]])],"derivedFrom":subQ3}),-1.0]])]});}
            var Q37;
            {var subQ1=sQuery(id+"F0.wireOp",EDGE,"E51.3");var subQ7=sQuery(id+"F0.wireOp",EDGE,"E5");var subQ8=makeQuery(id+"F0.imprint","INTERSECT",VERTEX,{"derivedFrom":[subQ7,subQ1]});Q37=makeQuery(id+"F0.imprint","IMPRINT",FACE,{"disambiguationData":[TD([[makeQuery(id+"F0.imprint","IMPRINT",EDGE,{"disambiguationData":[TD([[subQ8,-1.0]])],"derivedFrom":subQ7}),1.0]])]});}
            var Q38;
            {var subQ0=sQuery(id+"F0.wireOp",EDGE,"E51.4");var subQ1=sQuery(id+"F0.wireOp",EDGE,"E6");var subQ2=makeQuery(id+"F0.imprint","INTERSECT",VERTEX,{"derivedFrom":[subQ1,subQ0]});Q38=makeQuery(id+"F0.imprint","IMPRINT",FACE,{"disambiguationData":[TD([[makeQuery(id+"F0.imprint","IMPRINT",EDGE,{"disambiguationData":[TD([[subQ2,-1.0]])],"derivedFrom":subQ1}),1.0]])]});}
            var Q39;
            {var subQ0=sQuery(id+"F0.wireOp",EDGE,"E51.4");var subQ1=sQuery(id+"F0.wireOp",EDGE,"E20");var subQ2=makeQuery(id+"F0.imprint","INTERSECT",VERTEX,{"derivedFrom":[subQ1,subQ0]});Q39=makeQuery(id+"F0.imprint","IMPRINT",FACE,{"disambiguationData":[TD([[makeQuery(id+"F0.imprint","IMPRINT",EDGE,{"disambiguationData":[TD([[subQ2,-1.0]])],"derivedFrom":subQ1}),-1.0]])]});}
            var Q40;
            {var subQ0=sQuery(id+"F0.wireOp",EDGE,"E52.5");var subQ1=sQuery(id+"F0.wireOp",EDGE,"E7");var subQ2=makeQuery(id+"F0.imprint","INTERSECT",VERTEX,{"derivedFrom":[subQ1,subQ0]});Q40=makeQuery(id+"F0.imprint","IMPRINT",FACE,{"disambiguationData":[TD([[makeQuery(id+"F0.imprint","IMPRINT",EDGE,{"disambiguationData":[TD([[subQ2,-1.0]])],"derivedFrom":subQ1}),1.0]])]});}
            var Q41;
            {var subQ1=sQuery(id+"F0.wireOp",EDGE,"E51.6");var subQ8=sQuery(id+"F0.wireOp",EDGE,"E36");var subQ10=makeQuery(id+"F0.imprint","INTERSECT",VERTEX,{"derivedFrom":[subQ8,subQ1]});Q41=makeQuery(id+"F0.imprint","IMPRINT",FACE,{"disambiguationData":[TD([[makeQuery(id+"F0.imprint","IMPRINT",EDGE,{"disambiguationData":[TD([[subQ10,-1.0]])],"derivedFrom":subQ8}),1.0]])]});}
            var Q42;
            {var subQ0=sQuery(id+"F0.wireOp",EDGE,"E51.7");var subQ1=sQuery(id+"F0.wireOp",EDGE,"E38");var subQ2=makeQuery(id+"F0.imprint","INTERSECT",VERTEX,{"derivedFrom":[subQ1,subQ0]});Q42=makeQuery(id+"F0.imprint","IMPRINT",FACE,{"disambiguationData":[TD([[makeQuery(id+"F0.imprint","IMPRINT",EDGE,{"disambiguationData":[TD([[subQ2,-1.0]])],"derivedFrom":subQ1}),1.0]])]});}
            var Q43;
            {var subQ0=sQuery(id+"F0.wireOp",EDGE,"E52.0");var subQ1=sQuery(id+"F0.wireOp",EDGE,"E39");var subQ2=makeQuery(id+"F0.imprint","INTERSECT",VERTEX,{"derivedFrom":[subQ1,subQ0]});Q43=makeQuery(id+"F0.imprint","IMPRINT",FACE,{"disambiguationData":[TD([[makeQuery(id+"F0.imprint","IMPRINT",EDGE,{"disambiguationData":[TD([[subQ2,-1.0]])],"derivedFrom":subQ1}),1.0]])]});}
            var Q44;
            {var subQ0=sQuery(id+"F0.wireOp",EDGE,"E52.7");var subQ1=sQuery(id+"F0.wireOp",EDGE,"E35");var subQ2=makeQuery(id+"F0.imprint","INTERSECT",VERTEX,{"derivedFrom":[subQ1,subQ0]});Q44=makeQuery(id+"F0.imprint","IMPRINT",FACE,{"disambiguationData":[TD([[makeQuery(id+"F0.imprint","IMPRINT",EDGE,{"disambiguationData":[TD([[subQ2,-1.0]])],"derivedFrom":subQ1}),1.0]])]});}
            var Q45;
            {var subQ0=sQuery(id+"F0.wireOp",EDGE,"E51.5");var subQ1=sQuery(id+"F0.wireOp",EDGE,"E11");var subQ2=makeQuery(id+"F0.imprint","INTERSECT",VERTEX,{"derivedFrom":[subQ1,subQ0]});Q45=makeQuery(id+"F0.imprint","IMPRINT",FACE,{"disambiguationData":[TD([[makeQuery(id+"F0.imprint","IMPRINT",EDGE,{"disambiguationData":[TD([[subQ2,-1.0]])],"derivedFrom":subQ1}),1.0]])]});}
            var Q46;
            {var subQ0=sQuery(id+"F0.wireOp",EDGE,"E51.5");var subQ1=sQuery(id+"F0.wireOp",EDGE,"E9");var subQ2=makeQuery(id+"F0.imprint","INTERSECT",VERTEX,{"derivedFrom":[subQ1,subQ0]});Q46=makeQuery(id+"F0.imprint","IMPRINT",FACE,{"disambiguationData":[TD([[makeQuery(id+"F0.imprint","IMPRINT",EDGE,{"disambiguationData":[TD([[subQ2,-1.0]])],"derivedFrom":subQ1}),1.0]])]});}
            var Q47;
            {var subQ5=sQuery(id+"F0.wireOp",EDGE,"E52.5");var subQ6=sQuery(id+"F0.wireOp",EDGE,"E7");var subQ7=makeQuery(id+"F0.imprint","INTERSECT",VERTEX,{"derivedFrom":[subQ6,subQ5]});Q47=makeQuery(id+"F0.imprint","IMPRINT",FACE,{"disambiguationData":[TD([[makeQuery(id+"F0.imprint","IMPRINT",EDGE,{"disambiguationData":[TD([[subQ7,-1.0]])],"derivedFrom":subQ6}),-1.0]])]});}
            var Q48;
            {var subQ3=sQuery(id+"F0.wireOp",EDGE,"E12");var subQ9=sQuery(id+"F0.wireOp",EDGE,"E52.6");var subQ10=makeQuery(id+"F0.imprint","INTERSECT",VERTEX,{"derivedFrom":[subQ3,subQ9]});Q48=makeQuery(id+"F0.imprint","IMPRINT",FACE,{"disambiguationData":[TD([[makeQuery(id+"F0.imprint","IMPRINT",EDGE,{"disambiguationData":[TD([[subQ10,-1.0]])],"derivedFrom":subQ3}),-1.0]])]});}
            var Q49;
            {var subQ0=sQuery(id+"F0.wireOp",EDGE,"E51.6");var subQ1=sQuery(id+"F0.wireOp",EDGE,"E14");var subQ2=makeQuery(id+"F0.imprint","INTERSECT",VERTEX,{"derivedFrom":[subQ1,subQ0]});Q49=makeQuery(id+"F0.imprint","IMPRINT",FACE,{"disambiguationData":[TD([[makeQuery(id+"F0.imprint","IMPRINT",EDGE,{"disambiguationData":[TD([[subQ2,-1.0]])],"derivedFrom":subQ1}),1.0]])]});}
            var Q50;
            {var subQ0=sQuery(id+"F0.wireOp",EDGE,"E51.7");var subQ1=sQuery(id+"F0.wireOp",EDGE,"E40");var subQ2=makeQuery(id+"F0.imprint","INTERSECT",VERTEX,{"derivedFrom":[subQ1,subQ0]});Q50=makeQuery(id+"F0.imprint","IMPRINT",FACE,{"disambiguationData":[TD([[makeQuery(id+"F0.imprint","IMPRINT",EDGE,{"disambiguationData":[TD([[subQ2,-1.0]])],"derivedFrom":subQ1}),1.0]])]});}
            var Q51;
            {var subQ0=sQuery(id+"F0.wireOp",EDGE,"E51.7");var subQ3=sQuery(id+"F0.wireOp",EDGE,"E42");var subQ4=makeQuery(id+"F0.imprint","INTERSECT",VERTEX,{"derivedFrom":[subQ3,subQ0]});Q51=makeQuery(id+"F0.imprint","IMPRINT",FACE,{"disambiguationData":[TD([[makeQuery(id+"F0.imprint","IMPRINT",EDGE,{"disambiguationData":[TD([[subQ4,-1.0]])],"derivedFrom":subQ3}),1.0]])]});}
            var Q52;
            {var subQ0=sQuery(id+"F0.wireOp",EDGE,"E51.0");var subQ1=sQuery(id+"F0.wireOp",EDGE,"E44");var subQ2=makeQuery(id+"F0.imprint","INTERSECT",VERTEX,{"derivedFrom":[subQ1,subQ0]});Q52=makeQuery(id+"F0.imprint","IMPRINT",FACE,{"disambiguationData":[TD([[makeQuery(id+"F0.imprint","IMPRINT",EDGE,{"disambiguationData":[TD([[subQ2,-1.0]])],"derivedFrom":subQ1}),1.0]])]});}
            var Q53;
            {var subQ0=sQuery(id+"F0.wireOp",EDGE,"E51.0");var subQ1=sQuery(id+"F0.wireOp",EDGE,"E34");var subQ2=makeQuery(id+"F0.imprint","INTERSECT",VERTEX,{"derivedFrom":[subQ1,subQ0]});Q53=makeQuery(id+"F0.imprint","IMPRINT",FACE,{"disambiguationData":[TD([[makeQuery(id+"F0.imprint","IMPRINT",EDGE,{"disambiguationData":[TD([[subQ2,-1.0]])],"derivedFrom":subQ1}),-1.0]])]});}
            var Q54;
            {var subQ0=sQuery(id+"F0.wireOp",EDGE,"E52.1");var subQ1=sQuery(id+"F0.wireOp",EDGE,"E31");var subQ2=makeQuery(id+"F0.imprint","INTERSECT",VERTEX,{"derivedFrom":[subQ1,subQ0]});Q54=makeQuery(id+"F0.imprint","IMPRINT",FACE,{"disambiguationData":[TD([[makeQuery(id+"F0.imprint","IMPRINT",EDGE,{"disambiguationData":[TD([[subQ2,-1.0]])],"derivedFrom":subQ1}),1.0]])]});}
            var Q55;
            {var subQ0=sQuery(id+"F0.wireOp",EDGE,"E51.1");var subQ3=sQuery(id+"F0.wireOp",EDGE,"E30");var subQ4=makeQuery(id+"F0.imprint","INTERSECT",VERTEX,{"derivedFrom":[subQ3,subQ0]});Q55=makeQuery(id+"F0.imprint","IMPRINT",FACE,{"disambiguationData":[TD([[makeQuery(id+"F0.imprint","IMPRINT",EDGE,{"disambiguationData":[TD([[subQ4,-1.0]])],"derivedFrom":subQ3}),-1.0]])]});}
            var Q56;
            {var subQ0=sQuery(id+"F0.wireOp",EDGE,"E51.1");var subQ1=sQuery(id+"F0.wireOp",EDGE,"E28");var subQ2=makeQuery(id+"F0.imprint","INTERSECT",VERTEX,{"derivedFrom":[subQ1,subQ0]});Q56=makeQuery(id+"F0.imprint","IMPRINT",FACE,{"disambiguationData":[TD([[makeQuery(id+"F0.imprint","IMPRINT",EDGE,{"disambiguationData":[TD([[subQ2,-1.0]])],"derivedFrom":subQ1}),-1.0]])]});}
            var Q57;
            {var subQ0=sQuery(id+"F0.wireOp",EDGE,"E51.1");var subQ1=sQuery(id+"F0.wireOp",EDGE,"E26");var subQ2=makeQuery(id+"F0.imprint","INTERSECT",VERTEX,{"derivedFrom":[subQ1,subQ0]});Q57=makeQuery(id+"F0.imprint","IMPRINT",FACE,{"disambiguationData":[TD([[makeQuery(id+"F0.imprint","IMPRINT",EDGE,{"disambiguationData":[TD([[subQ2,-1.0]])],"derivedFrom":subQ1}),-1.0]])]});}
            var Q58;
            {var subQ0=sQuery(id+"F0.wireOp",EDGE,"E51.1");var subQ1=sQuery(id+"F0.wireOp",EDGE,"E24");var subQ2=makeQuery(id+"F0.imprint","INTERSECT",VERTEX,{"derivedFrom":[subQ1,subQ0]});Q58=makeQuery(id+"F0.imprint","IMPRINT",FACE,{"disambiguationData":[TD([[makeQuery(id+"F0.imprint","IMPRINT",EDGE,{"disambiguationData":[TD([[subQ2,-1.0]])],"derivedFrom":subQ1}),-1.0]])]});}
            var Q59;
            {var subQ0=sQuery(id+"F0.wireOp",EDGE,"E51.2");var subQ3=sQuery(id+"F0.wireOp",EDGE,"E22");var subQ4=makeQuery(id+"F0.imprint","INTERSECT",VERTEX,{"derivedFrom":[subQ3,subQ0]});Q59=makeQuery(id+"F0.imprint","IMPRINT",FACE,{"disambiguationData":[TD([[makeQuery(id+"F0.imprint","IMPRINT",EDGE,{"disambiguationData":[TD([[subQ4,-1.0]])],"derivedFrom":subQ3}),-1.0]])]});}
            var Q60;
            {var subQ0=sQuery(id+"F0.wireOp",EDGE,"E51.2");var subQ1=sQuery(id+"F0.wireOp",EDGE,"E19");var subQ2=makeQuery(id+"F0.imprint","INTERSECT",VERTEX,{"derivedFrom":[subQ1,subQ0]});Q60=makeQuery(id+"F0.imprint","IMPRINT",FACE,{"disambiguationData":[TD([[makeQuery(id+"F0.imprint","IMPRINT",EDGE,{"disambiguationData":[TD([[subQ2,-1.0]])],"derivedFrom":subQ1}),-1.0]])]});}
            extrude(context, id + "F2", {"entities" : qUnion([Q0, Q1, Q2, Q3, Q4, Q5, Q6, Q7, Q8, Q9, Q10, Q11, Q12, Q13, Q14, Q15, Q16, Q17, Q18, Q19, Q20, Q21, Q22, Q23, Q24, Q25, Q26, Q27, Q28, Q29, Q30, Q31, Q32, Q33, Q34, Q35, Q36, Q37, Q38, Q39, Q40, Q41, Q42, Q43, Q44, Q45, Q46, Q47, Q48, Q49, Q50, Q51, Q52, Q53, Q54, Q55, Q56, Q57, Q58, Q59, Q60]), "depth" : 25.4 * mm});
        }
    });
